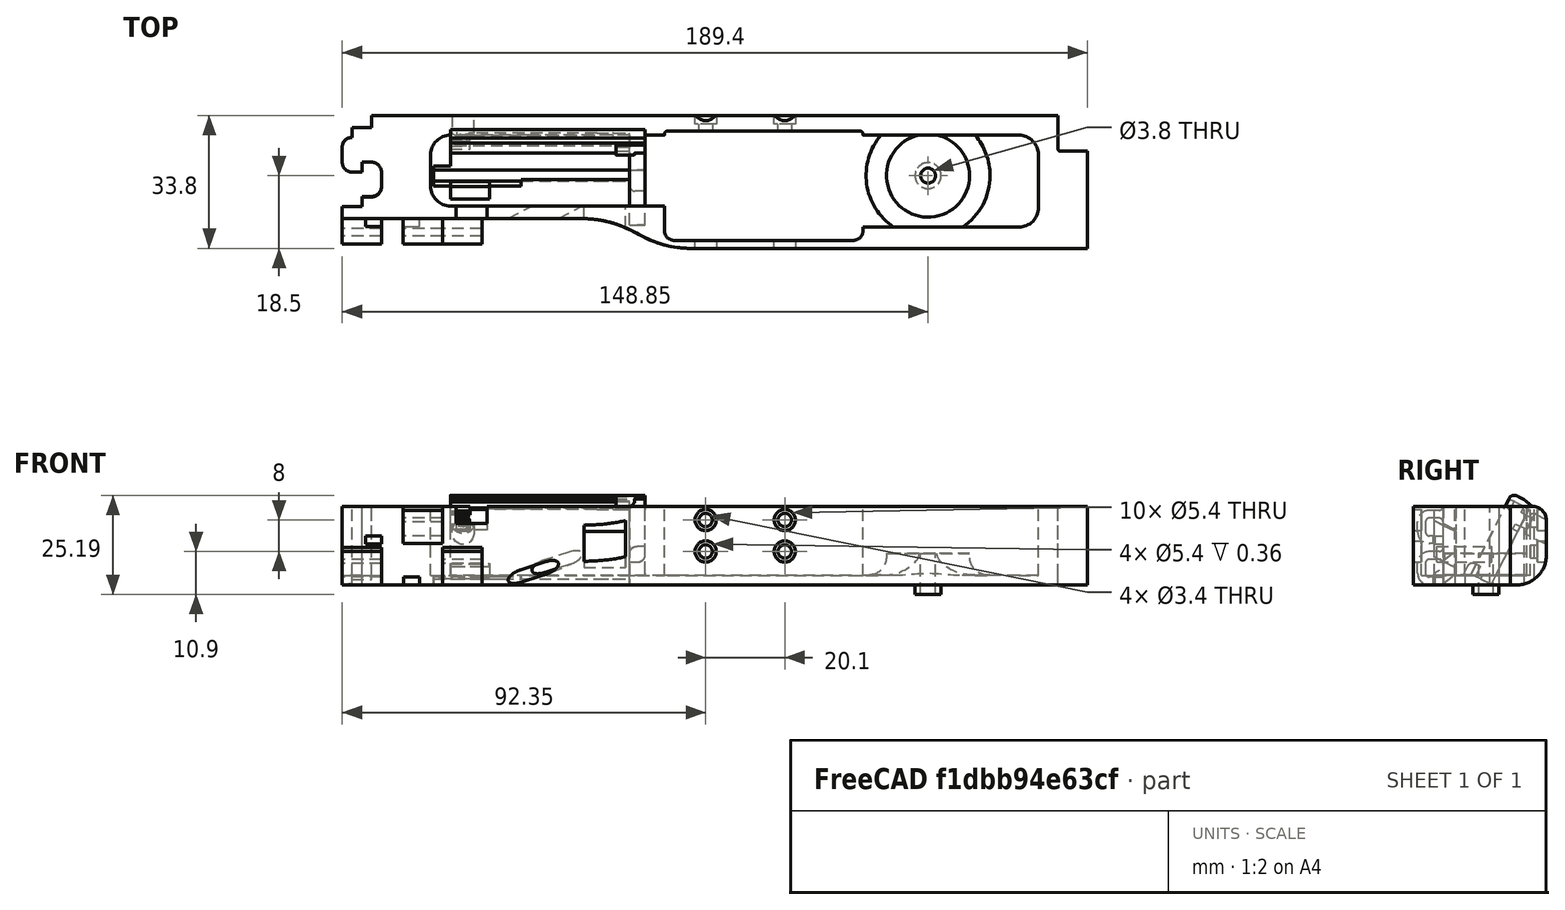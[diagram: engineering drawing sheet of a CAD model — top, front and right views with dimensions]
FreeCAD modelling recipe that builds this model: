
FCSTD DOCUMENT  (FreeCAD 0.19R0.19.2)
Label: v0_9994
License: All rights reserved
LicenseURL: http://en.wikipedia.org/wiki/All_rights_reserved
objects: Sketcher::SketchObject×44, Part::Extrusion×35, Part::MultiFuse×22, Part::Box×18, Part::Cut×15, Part::Fillet×13, App::MeasureDistance×10, Part::Cylinder×4, Part::Revolution×1, Mesh::Feature×1
note: 152 computed .brp shape members not serialized (recipe doc carries the construction recipe); baked Part::Feature solids carry a one-line shape summary decoded from their .brp

FEATURE [Sketcher::SketchObject] Sketch
  FullyConstrained = true
  sketch-geometry (36):
    g0: LineSegment StartX=0 StartY=0 StartZ=0 EndX=154.4 EndY=0 EndZ=0
    g1: LineSegment StartX=154.4 StartY=0 StartZ=0 EndX=154.4 EndY=-7.6 EndZ=0
    g2: LineSegment StartX=32.5209 StartY=-26.2 StartZ=0 EndX=-7.5 EndY=-26.2 EndZ=0
    g3-g7: Circle x5 (B-spline internal-alignment scaffolding for g8; pole/knot coordinates omitted)
    g8: BSplineCurve PolesCount=5 KnotsCount=3 Degree=3 IsPeriodic=0
    g9: GeomPoint X=61.85 Y=-33.8 Z=0
    g10: GeomPoint X=47.185 Y=-29.9 Z=0
    g11: GeomPoint X=32.5209 Y=-26.2 Z=0
    g12: Circle CenterX=121.35 CenterY=-14.3 CenterZ=0 NormalX=0 NormalY=0 NormalZ=1 AngleXU=0 Radius=3.25
    g13: LineSegment StartX=-7.5 StartY=-26.2 StartZ=0 EndX=-27.5 EndY=-26.2 EndZ=0
    g14: LineSegment StartX=-20 StartY=0 StartZ=0 EndX=0 EndY=0 EndZ=0
    g15: LineSegment StartX=-25 StartY=-3.1 StartZ=0 EndX=-20 EndY=-3.1 EndZ=0
    g16: LineSegment StartX=-25 StartY=-3.1 StartZ=0 EndX=-25 EndY=-5.6 EndZ=0
    g17: LineSegment StartX=-27.5 StartY=-8.1 StartZ=0 EndX=-27.5 EndY=-11.85 EndZ=0
    g18: ArcOfCircle CenterX=-25 CenterY=-8.1 CenterZ=0 NormalX=0 NormalY=0 NormalZ=1 AngleXU=0 Radius=2.5 StartAngle=1.5708 EndAngle=3.14159
    g19: LineSegment StartX=-25 StartY=-14.35 StartZ=0 EndX=-22.5 EndY=-14.35 EndZ=0
    g20: ArcOfCircle CenterX=-25 CenterY=-11.85 CenterZ=0 NormalX=0 NormalY=0 NormalZ=1 AngleXU=0 Radius=2.5 StartAngle=3.14159 EndAngle=4.71239
    g21: LineSegment StartX=-22.5 StartY=-14.35 StartZ=0 EndX=-22.5 EndY=-11.85 EndZ=0
    g22: LineSegment StartX=-22.5 StartY=-11.85 StartZ=0 EndX=-20 EndY=-11.85 EndZ=0
    g23: ArcOfCircle CenterX=-20 CenterY=-14.35 CenterZ=0 NormalX=0 NormalY=0 NormalZ=1 AngleXU=0 Radius=2.5 StartAngle=8e-16 EndAngle=1.5708
    g24: LineSegment StartX=-17.5 StartY=-14.35 StartZ=0 EndX=-17.5 EndY=-18.1 EndZ=0
    g25: ArcOfCircle CenterX=-20 CenterY=-18.1 CenterZ=0 NormalX=0 NormalY=0 NormalZ=1 AngleXU=0 Radius=2.5 StartAngle=4.71239 EndAngle=6.28319
    g26: LineSegment StartX=-22.5 StartY=-20.6 StartZ=0 EndX=-20 EndY=-20.6 EndZ=0
    g27: LineSegment StartX=-22.5 StartY=-20.6 StartZ=0 EndX=-22.5 EndY=-23.1 EndZ=0
    g28: LineSegment StartX=-27.5 StartY=-23.1 StartZ=0 EndX=-22.5 EndY=-23.1 EndZ=0
    g29: LineSegment StartX=-20 StartY=-3.1 StartZ=0 EndX=-20 EndY=0 EndZ=0
    g30: LineSegment StartX=-27.5 StartY=-23.1 StartZ=0 EndX=-27.5 EndY=-26.2 EndZ=0
    g31: LineSegment StartX=154.4 StartY=-7.6 StartZ=0 EndX=154.4 EndY=-8.6 EndZ=0
    g32: ArcOfCircle CenterX=154.9 CenterY=-8.6 CenterZ=0 NormalX=0 NormalY=0 NormalZ=1 AngleXU=0 Radius=0.5 StartAngle=3.14159 EndAngle=4.71239
    g33: LineSegment StartX=154.9 StartY=-9.1 StartZ=0 EndX=161.9 EndY=-9.1 EndZ=0
    g34: LineSegment StartX=161.9 StartY=-9.1 StartZ=0 EndX=161.9 EndY=-33.8 EndZ=0
    g35: LineSegment StartX=161.9 StartY=-33.8 StartZ=0 EndX=61.85 EndY=-33.8 EndZ=0
  constraints (72):
    c: PointOnObject(g0,g-2)
    c: Horizontal(g0)
    c: Distance(g0) = 154.4
    c: DistanceY(g-1,g0) = 0
    c: Vertical(g1)
    c: Distance(g1) = 7.6
    c: Coincident(g1,g0)
    c: Horizontal(g2)
    c: Block(g2)
    c: Weight(g3) = 1
    c: Coincident(g8,g2)
    c: InternalAlignment(g3-g7 -> g8) x5
    c: InternalAlignment(g9,g8)
    c: InternalAlignment(g10,g8)
    c: InternalAlignment(g11,g8)
    c: Block(g12)
    c: Coincident(g13,g2)
    c: Horizontal(g13)
    c: Distance(g13) = 20
    c: Horizontal(g14)
    c: Distance(g14) = 20
    c: Coincident(g14,g0)
    c: Horizontal(g15)
    c: Vertical(g16)
    c: Coincident(g16,g15)
    c: Vertical(g17)
    c: Coincident(g18,g16)
    c: Block(g18)
    c: Coincident(g17,g18)
    c: Horizontal(g19)
    c: Coincident(g20,g17)
    c: Block(g20)
    c: Block(g19)
    c: Vertical(g21)
    c: Coincident(g21,g19)
    c: Horizontal(g22)
    c: Coincident(g22,g21)
    c: Coincident(g23,g22)
    c: Vertical(g24)
    c: Block(g23)
    c: Coincident(g24,g23)
    c: Coincident(g25,g24)
    c: Block(g25)
    c: Horizontal(g26)
    c: Coincident(g26,g25)
    c: Vertical(g27)
    c: Coincident(g27,g26)
    c: Horizontal(g28)
    c: Coincident(g28,g27)
    c: Block(g15)
    c: Block(g28)
    c: Coincident(g29,g15)
    c: Coincident(g29,g14)
    c: Vertical(g29)
    c: Coincident(g30,g28)
    c: Coincident(g30,g13)
    c: Vertical(g30)
    c: Vertical(g31)
    c: Distance(g31) = 1
    c: Coincident(g31,g1)
    c: Coincident(g32,g31)
    c: Block(g32)
    c: Coincident(g33,g32)
    c: Horizontal(g33)
    c: Coincident(g34,g33)
    c: Vertical(g34)
    c: Block(g34)
    c: Coincident(g35,g34)
    c: Horizontal(g35)
    c: Block(g35)
    c: Coincident(g8,g35)
    c: Block(g8)
FEATURE [Part::Extrusion] Extrude  label="mainBodyBaseExtrude"
  Base = -> Sketch
  Dir = (0,0,1)
  DirMode = 2
  FaceMakerClass = Part::FaceMakerBullseye
  LengthFwd = 2.4
  LengthRev = 0
  Solid = true
  Symmetric = false
FEATURE [Sketcher::SketchObject] Sketch001
  FullyConstrained = true
  sketch-geometry (75):
    g0: ArcOfCircle CenterX=144.4 CenterY=-10 CenterZ=0 NormalX=0 NormalY=0 NormalZ=1 AngleXU=0 Radius=5 StartAngle=4.345e-13 EndAngle=1.5708
    g1: LineSegment StartX=32.5209 StartY=-26.2 StartZ=0 EndX=-7.49911 EndY=-26.2 EndZ=0
    g2: LineSegment StartX=0 StartY=0 StartZ=0 EndX=154.4 EndY=0 EndZ=0
    g3-g7: Circle x5 (B-spline internal-alignment scaffolding for g8; pole/knot coordinates omitted)
    g8: BSplineCurve PolesCount=5 KnotsCount=3 Degree=3 IsPeriodic=0
    g9: GeomPoint X=61.85 Y=-33.8 Z=0
    g10: GeomPoint X=47.1857 Y=-29.9 Z=0
    g11: GeomPoint X=32.5209 Y=-26.2 Z=0
    g12: LineSegment StartX=154.4 StartY=0 StartZ=0 EndX=154.4 EndY=-7.6 EndZ=0
    g13: LineSegment StartX=20 StartY=-5 StartZ=0 EndX=54.35 EndY=-5 EndZ=0
    g14: LineSegment StartX=104.85 StartY=-5 StartZ=0 EndX=144.4 EndY=-5 EndZ=0
    g15: LineSegment StartX=54.35 StartY=-23 StartZ=0 EndX=20 EndY=-23 EndZ=0
    g16: LineSegment StartX=-27.4991 StartY=-26.2 StartZ=0 EndX=-7.49911 EndY=-26.2 EndZ=0
    g17: LineSegment StartX=-20 StartY=0 StartZ=0 EndX=0 EndY=0 EndZ=0
    g18: LineSegment StartX=-27.4991 StartY=-23.2 StartZ=0 EndX=-22.5 EndY=-23.2 EndZ=0
    g19: LineSegment StartX=-22.5 StartY=-20.7 StartZ=0 EndX=-22.5 EndY=-23.2 EndZ=0
    g20: LineSegment StartX=-22.5 StartY=-20.7 StartZ=0 EndX=-20 EndY=-20.7 EndZ=0
    g21: ArcOfCircle CenterX=-20 CenterY=-18.2 CenterZ=0 NormalX=0 NormalY=0 NormalZ=1 AngleXU=0 Radius=2.5 StartAngle=4.71239 EndAngle=6.28319
    g22: LineSegment StartX=-17.5 StartY=-14.4 StartZ=0 EndX=-17.5 EndY=-18.2 EndZ=0
    g23: ArcOfCircle CenterX=-20 CenterY=-14.4 CenterZ=0 NormalX=0 NormalY=0 NormalZ=1 AngleXU=0 Radius=2.5 StartAngle=9e-16 EndAngle=1.5708
    g24: LineSegment StartX=-22.5 StartY=-11.9 StartZ=0 EndX=-20 EndY=-11.9 EndZ=0
    g25: LineSegment StartX=-22.5 StartY=-14.4 StartZ=0 EndX=-22.5 EndY=-11.9 EndZ=0
    g26: LineSegment StartX=-25 StartY=-14.4 StartZ=0 EndX=-22.5 EndY=-14.4 EndZ=0
    g27: ArcOfCircle CenterX=-25 CenterY=-11.9 CenterZ=0 NormalX=0 NormalY=0 NormalZ=1 AngleXU=0 Radius=2.5 StartAngle=3.14159 EndAngle=4.71239
    g28: LineSegment StartX=-27.5 StartY=-8.1 StartZ=0 EndX=-27.5 EndY=-11.9 EndZ=0
    g29: ArcOfCircle CenterX=-25 CenterY=-8.1 CenterZ=0 NormalX=0 NormalY=0 NormalZ=1 AngleXU=0 Radius=2.5 StartAngle=1.5708 EndAngle=3.14159
    g30: LineSegment StartX=-25 StartY=-3.1 StartZ=0 EndX=-25 EndY=-5.6 EndZ=0
    g31: LineSegment StartX=-20 StartY=-3.1 StartZ=0 EndX=-25 EndY=-3.1 EndZ=0
    g32: LineSegment StartX=-20 StartY=0 StartZ=0 EndX=-20 EndY=-3.1 EndZ=0
    g33: LineSegment StartX=-27.4991 StartY=-26.2 StartZ=0 EndX=-27.4991 EndY=-23.2 EndZ=0
    g34: LineSegment StartX=4.09e-14 StartY=-5 StartZ=0 EndX=20 EndY=-5 EndZ=0
    g35: ArcOfCircle CenterX=7.1e-15 CenterY=-18 CenterZ=0 NormalX=0 NormalY=0 NormalZ=1 AngleXU=0 Radius=5 StartAngle=3.14159 EndAngle=4.71239
    g36: ArcOfCircle CenterX=4.26e-14 CenterY=-10 CenterZ=0 NormalX=0 NormalY=0 NormalZ=1 AngleXU=0 Radius=5 StartAngle=1.5708 EndAngle=3.14159
    g37: LineSegment StartX=-5 StartY=-18 StartZ=0 EndX=-5 EndY=-10 EndZ=0
    g38: LineSegment StartX=6.2e-15 StartY=-23 StartZ=0 EndX=20 EndY=-23 EndZ=0
    g39: LineSegment StartX=154.4 StartY=-7.6 StartZ=0 EndX=154.4 EndY=-8.6 EndZ=0
    g40: LineSegment StartX=154.9 StartY=-9.1 StartZ=0 EndX=161.9 EndY=-9.1 EndZ=0
    g41: ArcOfCircle CenterX=154.9 CenterY=-8.6 CenterZ=0 NormalX=0 NormalY=0 NormalZ=1 AngleXU=0 Radius=0.5 StartAngle=3.14159 EndAngle=4.71299
    g42: LineSegment StartX=104.85 StartY=-28.3916 StartZ=0 EndX=144.408 EndY=-28.3916 EndZ=0
    g43: LineSegment StartX=149.4 StartY=-10 StartZ=0 EndX=149.4 EndY=-23.4 EndZ=0
    g44: ArcOfCircle CenterX=144.408 CenterY=-23.4 CenterZ=0 NormalX=0 NormalY=0 NormalZ=1 AngleXU=0 Radius=4.99164 StartAngle=4.71239 EndAngle=6.28319
    g45: LineSegment StartX=104.85 StartY=-28.3916 StartZ=0 EndX=104.85 EndY=-28.7833 EndZ=0
    g46: LineSegment StartX=54.35 StartY=-28.7916 StartZ=0 EndX=54.35 EndY=-23 EndZ=0
    g47: LineSegment StartX=161.9 StartY=-33.8 StartZ=0 EndX=161.9 EndY=-9.1 EndZ=0
    g48: LineSegment StartX=61.85 StartY=-33.8 StartZ=0 EndX=161.9 EndY=-33.8 EndZ=0
    g49: Circle CenterX=54.35 CenterY=-28.7916 CenterZ=0 NormalX=0 NormalY=0 NormalZ=1 AngleXU=0 Radius=1
    g50: Circle CenterX=54.35 CenterY=-31.7916 CenterZ=0 NormalX=0 NormalY=0 NormalZ=1 AngleXU=0 Radius=1
    g51: Circle CenterX=57.35 CenterY=-31.7916 CenterZ=0 NormalX=0 NormalY=0 NormalZ=1 AngleXU=0 Radius=1
    g52: BSplineCurve PolesCount=3 KnotsCount=2 Degree=2 IsPeriodic=0
    g53: GeomPoint X=54.35 Y=-28.7916 Z=0
    g54: GeomPoint X=57.35 Y=-31.7916 Z=0
    g55: Circle CenterX=104.85 CenterY=-28.7833 CenterZ=0 NormalX=0 NormalY=0 NormalZ=1 AngleXU=0 Radius=1
    g56: Circle CenterX=104.85 CenterY=-31.7916 CenterZ=0 NormalX=0 NormalY=0 NormalZ=1 AngleXU=0 Radius=1
    g57: Circle CenterX=101.85 CenterY=-31.7916 CenterZ=0 NormalX=0 NormalY=0 NormalZ=1 AngleXU=0 Radius=1
    g58: BSplineCurve PolesCount=3 KnotsCount=2 Degree=2 IsPeriodic=0
    g59: GeomPoint X=104.85 Y=-28.7833 Z=0
    g60: GeomPoint X=101.85 Y=-31.7916 Z=0
    g61: LineSegment StartX=57.35 StartY=-31.7916 StartZ=0 EndX=101.85 EndY=-31.7916 EndZ=0
    g62: Circle CenterX=54.35 CenterY=-5 CenterZ=0 NormalX=0 NormalY=0 NormalZ=1 AngleXU=0 Radius=1
    g63: Circle CenterX=54.35 CenterY=-4 CenterZ=0 NormalX=0 NormalY=0 NormalZ=1 AngleXU=0 Radius=1
    g64: Circle CenterX=55.15 CenterY=-4 CenterZ=0 NormalX=0 NormalY=0 NormalZ=1 AngleXU=0 Radius=1
    g65: BSplineCurve PolesCount=3 KnotsCount=2 Degree=2 IsPeriodic=0
    g66: GeomPoint X=54.35 Y=-5 Z=0
    g67: GeomPoint X=55.15 Y=-4 Z=0
    g68: Circle CenterX=104.85 CenterY=-5 CenterZ=0 NormalX=0 NormalY=0 NormalZ=1 AngleXU=0 Radius=1
    g69: Circle CenterX=104.85 CenterY=-4 CenterZ=0 NormalX=0 NormalY=0 NormalZ=1 AngleXU=0 Radius=1
    g70: Circle CenterX=104.05 CenterY=-4 CenterZ=0 NormalX=0 NormalY=0 NormalZ=1 AngleXU=0 Radius=1
    g71: BSplineCurve PolesCount=3 KnotsCount=2 Degree=2 IsPeriodic=0
    g72: GeomPoint X=104.85 Y=-5 Z=0
    g73: GeomPoint X=104.05 Y=-4 Z=0
    g74: LineSegment StartX=104.05 StartY=-4 StartZ=0 EndX=55.15 EndY=-4 EndZ=0
  constraints (156):
    c: PointOnObject(g2,g-2)
    c: DistanceY(g-1,g2) = 0
    c: Block(g0)
    c: Horizontal(g1)
    c: Distance(g1) = 40.02
    c: Horizontal(g2)
    c: Block(g2)
    c: Weight(g3) = 1
    c: Equal(g3, g4-g7) x4
    c: Coincident(g8,g1)
    c: InternalAlignment(g3-g7 -> g8) x5
    c: InternalAlignment(g9,g8)
    c: InternalAlignment(g10,g8)
    c: InternalAlignment(g11,g8)
    c: Vertical(g12)
    c: Coincident(g12,g2)
    c: Distance(g12) = 7.6
    c: Block(g12)
    c: Horizontal(g13)
    c: Coincident(g14,g0)
    c: Horizontal(g14)
    c: Horizontal(g15)
    c: Horizontal(g16)
    c: Distance(g16) = 20
    c: Coincident(g1,g16)
    c: Horizontal(g17)
    c: Distance(g17) = 20
    c: Coincident(g17,g2)
    c: Horizontal(g31)
    c: Vertical(g30)
    c: Coincident(g29,g30)
    c: Vertical(g28)
    c: Block(g29)
    c: Coincident(g27,g28)
    c: Block(g27)
    c: Horizontal(g26)
    c: Coincident(g26,g27)
    c: Vertical(g25)
    c: Coincident(g25,g26)
    c: Horizontal(g24)
    c: Coincident(g23,g24)
    c: Block(g23)
    c: Vertical(g22)
    c: Coincident(g21,g22)
    c: Block(g21)
    c: Horizontal(g20)
    c: Coincident(g20,g21)
    c: Vertical(g19)
    c: Coincident(g19,g20)
    c: Horizontal(g18)
    c: Coincident(g18,g19)
    c: Coincident(g32,g17)
    c: Coincident(g32,g31)
    c: Vertical(g32)
    c: Coincident(g33,g16)
    c: Coincident(g33,g18)
    c: Vertical(g33)
    c: Block(g33)
    c: Block(g18)
    c: Block(g22)
    c: Block(g26)
    c: Block(g25)
    c: Block(g24)
    c: Block(g28)
    c: Block(g31)
    c: Block(g30)
    c: Horizontal(g34)
    c: Distance(g34) = 20
    c: Block(g35)
    c: Block(g36)
    c: Coincident(g37,g35)
    c: Coincident(g37,g36)
    c: Vertical(g37)
    c: Coincident(g38,g35)
    c: Coincident(g38,g15)
    c: Horizontal(g38)
    c: Block(g38)
    c: Block(g34)
    c: Block(g13)
    c: Vertical(g39)
    c: Distance(g39) = 1
    c: Coincident(g39,g12)
    c: Horizontal(g40)
    c: Coincident(g41,g39)
    c: Coincident(g41,g40)
    c: Block(g39)
    c: Block(g41)
    c: Horizontal(g42)
    c: Vertical(g43)
    c: Distance(g43) = 13.4
    c: Coincident(g43,g0)
    c: Block(g42)
    c: Block(g43)
    c: Coincident(g44,g43)
    c: Coincident(g44,g42)
    c: Block(g44)
    c: Distance(g15) = 34.35
    c: Coincident(g45,g42)
    c: Vertical(g45)
    c: Coincident(g46,g15)
    c: Vertical(g46)
    c: Coincident(g47,g40)
    c: Vertical(g47)
    c: Block(g47)
    c: Coincident(g48,g47)
    c: Horizontal(g48)
    c: Block(g48)
    c: Coincident(g8,g48)
    c: Block(g8)
    c: Coincident(g52,g46)
    c: Weight(g49) = 1
    c: Equal(g49,g50)
    c: Equal(g49,g51)
    c: InternalAlignment(g49,g52)
    c: InternalAlignment(g50,g52)
    c: InternalAlignment(g51,g52)
    c: InternalAlignment(g53,g52)
    c: InternalAlignment(g54,g52)
    c: Coincident(g58,g45)
    c: Weight(g55) = 1
    c: Equal(g55,g56)
    c: Equal(g55,g57)
    c: InternalAlignment(g55,g58)
    c: InternalAlignment(g56,g58)
    c: InternalAlignment(g57,g58)
    c: InternalAlignment(g59,g58)
    c: InternalAlignment(g60,g58)
    c: Block(g58)
    c: Block(g52)
    c: Coincident(g61,g52)
    c: Coincident(g61,g58)
    c: Horizontal(g61)
    c: Block(g14)
    c: Coincident(g65,g13)
    c: Weight(g62) = 1
    c: Equal(g62,g63)
    c: Equal(g62,g64)
    c: InternalAlignment(g62,g65)
    c: InternalAlignment(g63,g65)
    c: InternalAlignment(g64,g65)
    c: InternalAlignment(g66,g65)
    c: InternalAlignment(g67,g65)
    c: Block(g65)
    c: Coincident(g71,g14)
    c: Weight(g68) = 1
    c: Equal(g68,g69)
    c: Equal(g68,g70)
    c: InternalAlignment(g68,g71)
    c: InternalAlignment(g69,g71)
    c: InternalAlignment(g70,g71)
    c: InternalAlignment(g72,g71)
    c: InternalAlignment(g73,g71)
    c: Block(g71)
    c: Coincident(g74,g71)
    c: Coincident(g74,g65)
    c: Horizontal(g74)
FEATURE [Sketcher::SketchObject] Sketch005
  FullyConstrained = true
  Placement = pos=(0,0,0) rot=(1,0,0;1.5708rad)
  sketch-geometry (4):
    g0: Circle CenterX=84.95 CenterY=16.5 CenterZ=0 NormalX=0 NormalY=0 NormalZ=1 AngleXU=0 Radius=1.7
    g1: Circle CenterX=84.95 CenterY=8.5 CenterZ=0 NormalX=0 NormalY=0 NormalZ=1 AngleXU=0 Radius=1.7
    g2: Circle CenterX=64.85 CenterY=8.5 CenterZ=0 NormalX=0 NormalY=0 NormalZ=1 AngleXU=0 Radius=1.7
    g3: Circle CenterX=64.85 CenterY=16.5 CenterZ=0 NormalX=0 NormalY=0 NormalZ=1 AngleXU=0 Radius=1.7
  constraints (4):
    c: Block(g0)
    c: Block(g1)
    c: Block(g2)
    c: Block(g3)
FEATURE [Part::Extrusion] Extrude004  label="removeFromMainBodyToCreateScrewHolesForSolenoidExtrude004"
  Base = -> Sketch005
  Dir = (0,-1,1.1e-15)
  DirMode = 2
  FaceMakerClass = Part::FaceMakerBullseye
  LengthFwd = 10
  LengthRev = 0
  Solid = true
  Symmetric = false
FEATURE [Sketcher::SketchObject] Sketch004
  FullyConstrained = true
  Placement = pos=(0,0,0) rot=(1,0,0;1.5708rad)
  sketch-geometry (12):
    g0: LineSegment StartX=15.75 StartY=2.5 StartZ=0 EndX=15.75 EndY=0 EndZ=0
    g1: Circle CenterX=15.75 CenterY=2.5 CenterZ=0 NormalX=0 NormalY=0 NormalZ=1 AngleXU=0 Radius=1
    g2: Circle CenterX=10.55 CenterY=2.5 CenterZ=0 NormalX=0 NormalY=0 NormalZ=1 AngleXU=0 Radius=1
    g3: Circle CenterX=10.55 CenterY=8 CenterZ=0 NormalX=0 NormalY=0 NormalZ=1 AngleXU=0 Radius=1
    g4: BSplineCurve PolesCount=3 KnotsCount=2 Degree=2 IsPeriodic=0
    g5: GeomPoint X=15.75 Y=2.5 Z=0
    g6: GeomPoint X=10.55 Y=8 Z=0
    g7: LineSegment StartX=1.9 StartY=8 StartZ=0 EndX=10.55 EndY=8 EndZ=0
    g8: LineSegment StartX=1.9 StartY=-2.4 StartZ=0 EndX=1.9 EndY=8 EndZ=0
    g9: LineSegment StartX=3.30092 StartY=-2.4 StartZ=0 EndX=3.30092 EndY=0 EndZ=0
    g10: LineSegment StartX=15.75 StartY=0 StartZ=0 EndX=3.30092 EndY=0 EndZ=0
    g11: LineSegment StartX=3.30092 StartY=-2.4 StartZ=0 EndX=1.9 EndY=-2.4 EndZ=0
  constraints (26):
    c: Vertical(g0)
    c: Distance(g0) = 2.5
    c: Coincident(g4,g0)
    c: Weight(g1) = 1
    c: Equal(g1,g2)
    c: Equal(g1,g3)
    c: InternalAlignment(g1,g4)
    c: InternalAlignment(g2,g4)
    c: InternalAlignment(g3,g4)
    c: InternalAlignment(g5,g4)
    c: InternalAlignment(g6,g4)
    c: Block(g4)
    c: Coincident(g7,g4)
    c: Horizontal(g7)
    c: Vertical(g8)
    c: Coincident(g8,g7)
    c: Block(g8)
    c: Vertical(g9)
    c: Coincident(g10,g0)
    c: PointOnObject(g10,g-1)
    c: Horizontal(g10)
    c: Coincident(g10,g9)
    c: Block(g9)
    c: Coincident(g11,g9)
    c: Coincident(g11,g8)
    c: Horizontal(g11)
FEATURE [Sketcher::SketchObject] Sketch007
  FullyConstrained = true
  Placement = pos=(0,-14.3,2.37) rot=(-1,0,0;2.03453rad)
  sketch-geometry (6):
    g0: LineSegment StartX=0 StartY=0 StartZ=0 EndX=45.5 EndY=0 EndZ=0
    g1: LineSegment StartX=0 StartY=0 StartZ=0 EndX=0 EndY=-21.2 EndZ=0
    g2: LineSegment StartX=45.5 StartY=0 StartZ=0 EndX=49.5 EndY=0 EndZ=0
    g3: LineSegment StartX=49.5 StartY=0 StartZ=0 EndX=49.5 EndY=-21.2 EndZ=0
    g4: LineSegment StartX=49.5 StartY=-21.2 StartZ=0 EndX=0 EndY=-21.2 EndZ=0
    g5: Circle CenterX=3.25 CenterY=-18.05 CenterZ=0 NormalX=0 NormalY=0 NormalZ=1 AngleXU=0 Radius=1.6
  constraints (15):
    c: Coincident(g0,g-1)
    c: Horizontal(g0)
    c: Distance(g0) = 45.5
    c: Coincident(g1,g0)
    c: Vertical(g1)
    c: Horizontal(g2)
    c: Distance(g2) = 4
    c: Coincident(g2,g0)
    c: Coincident(g3,g2)
    c: Vertical(g3)
    c: Block(g3)
    c: Coincident(g4,g3)
    c: Horizontal(g4)
    c: Coincident(g4,g1)
    c: Block(g5)
FEATURE [Part::Extrusion] Extrude005  label="solenoidDriverHolderExtrude005"
  Base = -> Sketch007
  Dir = (0,0.894389,-0.447291)
  DirMode = 2
  FaceMakerClass = Part::FaceMakerBullseye
  LengthFwd = 10
  LengthRev = 0
  Placement = pos=(0,0,-2) rot=(0,0,1;0rad)
  Solid = true
  Symmetric = false
FEATURE [Sketcher::SketchObject] Sketch008
  FullyConstrained = false
  Placement = pos=(0,-4.3,-2.6) rot=(-1,0,0;2.03453rad)
  sketch-geometry (1):
    g0: Circle CenterX=42.25 CenterY=-3.15 CenterZ=0 NormalX=0 NormalY=0 NormalZ=1 AngleXU=0 Radius=4.5
FEATURE [Sketcher::SketchObject] Sketch009
  FullyConstrained = true
  Placement = pos=(0,-4.3,-2.6) rot=(-1,0,0;2.03453rad)
  sketch-geometry (1):
    g0: Circle CenterX=3.25 CenterY=-18.0217 CenterZ=0 NormalX=0 NormalY=0 NormalZ=1 AngleXU=0 Radius=2.8
  constraints (1):
    c: Block(g0)
FEATURE [Sketcher::SketchObject] Sketch010
  FullyConstrained = true
  Placement = pos=(0,-14.3,2.37) rot=(-1,0,0;2.03453rad)
  sketch-geometry (1):
    g0: Circle CenterX=3.25 CenterY=-18.05 CenterZ=0 NormalX=0 NormalY=0 NormalZ=1 AngleXU=0 Radius=1.6
  constraints (1):
    c: Block(g0)
FEATURE [Part::Extrusion] Extrude008  label="removeFromScrewHole3"
  Base = -> Sketch010
  Dir = (0,0.894389,-0.447291)
  DirMode = 2
  FaceMakerClass = Part::FaceMakerBullseye
  LengthFwd = -25
  LengthRev = 0
  Placement = pos=(0,4,-4) rot=(0,0,1;0rad)
  Solid = true
  Symmetric = false
FEATURE [Sketcher::SketchObject] Sketch011
  FullyConstrained = true
  Placement = pos=(0,-14.3,2.37) rot=(-1,0,0;2.03453rad)
  sketch-geometry (4):
    g0: LineSegment StartX=49.5 StartY=-21.2 StartZ=0 EndX=49.5 EndY=-22.8 EndZ=0
    g1: LineSegment StartX=49.5 StartY=-22.8 StartZ=0 EndX=0.002238 EndY=-22.8 EndZ=0
    g2: LineSegment StartX=0.002238 StartY=-21.2 StartZ=0 EndX=0.002238 EndY=-22.8 EndZ=0
    g3: LineSegment StartX=49.5 StartY=-21.2 StartZ=0 EndX=0.002238 EndY=-21.2 EndZ=0
  constraints (10):
    c: Vertical(g0)
    c: Distance(g0) = 1.6
    c: Coincident(g1,g0)
    c: Horizontal(g1)
    c: Vertical(g2)
    c: Coincident(g2,g1)
    c: Coincident(g3,g0)
    c: Coincident(g3,g2)
    c: Horizontal(g3)
    c: Block(g3)
FEATURE [Part::Extrusion] Extrude009  label="solenoidDriverTopLipFront"
  Base = -> Sketch011
  Dir = (0,0.894389,-0.447291)
  DirMode = 2
  FaceMakerClass = Part::FaceMakerBullseye
  LengthFwd = -2
  LengthRev = 0
  Placement = pos=(0,-2.9,-0.35) rot=(0,0,1;0rad)
  Solid = true
  Symmetric = false
FEATURE [Sketcher::SketchObject] Sketch012
  FullyConstrained = true
  Placement = pos=(0,-14.3,2.37) rot=(-1,0,0;2.03453rad)
  sketch-geometry (4):
    g0: LineSegment StartX=49.5 StartY=-21.2 StartZ=0 EndX=49.5 EndY=-22.8 EndZ=0
    g1: LineSegment StartX=49.5 StartY=-22.8 StartZ=0 EndX=0.002238 EndY=-22.8 EndZ=0
    g2: LineSegment StartX=0.002238 StartY=-21.2 StartZ=0 EndX=0.002238 EndY=-22.8 EndZ=0
    g3: LineSegment StartX=49.5 StartY=-21.2 StartZ=0 EndX=0.002238 EndY=-21.2 EndZ=0
  constraints (10):
    c: Vertical(g0)
    c: Distance(g0) = 1.6
    c: Coincident(g1,g0)
    c: Horizontal(g1)
    c: Vertical(g2)
    c: Coincident(g2,g1)
    c: Coincident(g3,g0)
    c: Coincident(g3,g2)
    c: Horizontal(g3)
    c: Block(g3)
FEATURE [Part::Extrusion] Extrude010  label="solenoidDriverTopLipLowerExtrude010"
  Base = -> Sketch012
  Dir = (0,0.894389,-0.447291)
  DirMode = 2
  FaceMakerClass = Part::FaceMakerBullseye
  LengthFwd = 5.05
  LengthRev = 0
  Solid = true
  Symmetric = false
FEATURE [Sketcher::SketchObject] Sketch015
  FullyConstrained = true
  Placement = pos=(0,-14.3,2.37) rot=(-1,0,0;2.03453rad)
  sketch-geometry (4):
    g0: LineSegment StartX=0 StartY=1.5 StartZ=0 EndX=0 EndY=0 EndZ=0
    g1: LineSegment StartX=0 StartY=1.5 StartZ=0 EndX=5 EndY=1.5 EndZ=0
    g2: LineSegment StartX=5 StartY=1.5 StartZ=0 EndX=5 EndY=0 EndZ=0
    g3: LineSegment StartX=0 StartY=0 StartZ=0 EndX=5 EndY=0 EndZ=0
  constraints (13):
    c: Vertical(g0)
    c: Distance(g0) = 1.5
    c: Horizontal(g1)
    c: Distance(g1) = 5
    c: Coincident(g1,g0)
    c: Vertical(g2)
    c: Distance(g2) = 1.5
    c: Coincident(g2,g1)
    c: Block(g1)
    c: Block(g2)
    c: Block(g0)
    c: Coincident(g3,g0)
    c: Coincident(g3,g2)
FEATURE [Part::Extrusion] Extrude013  label="solenoidDriverBottomLipTopExtrude012"
  Base = -> Sketch015
  Dir = (0,0.894389,-0.447291)
  DirMode = 2
  FaceMakerClass = Part::FaceMakerBullseye
  LengthFwd = -6.5
  LengthRev = 0
  Placement = pos=(0,-14.15,19.65) rot=(1,0,0;1.5708rad)
  Solid = true
  Symmetric = false
FEATURE [Sketcher::SketchObject] Sketch016
  FullyConstrained = true
  Placement = pos=(0,0,0) rot=(1,0,0;1.5708rad)
  sketch-geometry (4):
    g0: Circle CenterX=84.15 CenterY=16.5 CenterZ=0 NormalX=0 NormalY=0 NormalZ=1 AngleXU=0 Radius=2.7
    g1: Circle CenterX=64.05 CenterY=16.5 CenterZ=0 NormalX=0 NormalY=0 NormalZ=1 AngleXU=0 Radius=2.7
    g2: Circle CenterX=64.05 CenterY=8.5 CenterZ=0 NormalX=0 NormalY=0 NormalZ=1 AngleXU=0 Radius=2.7
    g3: Circle CenterX=84.15 CenterY=8.5 CenterZ=0 NormalX=0 NormalY=0 NormalZ=1 AngleXU=0 Radius=2.7
  constraints (4):
    c: Block(g0)
    c: Block(g1)
    c: Block(g3)
    c: Block(g2)
FEATURE [Part::Extrusion] Extrude014  label="removeFromMainBodyToCreateScrewHoleCounterSinks"
  Base = -> Sketch016
  Dir = (0,-1,1.1e-15)
  DirMode = 2
  FaceMakerClass = Part::FaceMakerBullseye
  LengthFwd = 1.9
  LengthRev = 0
  Placement = pos=(0.8,-0.36,0) rot=(0,0,1;0rad)
  Solid = true
  Symmetric = false
FEATURE [Part::Extrusion] Extrude015  label="removeFromScrewHole2Extrude007"
  Base = -> Sketch009
  Dir = (0,0.894389,-0.447291)
  DirMode = 2
  FaceMakerClass = Part::FaceMakerBullseye
  LengthFwd = 10
  LengthRev = 0
  Placement = pos=(0,-8,2) rot=(0,0,1;0rad)
  Solid = true
  Symmetric = false
FEATURE [Sketcher::SketchObject] Sketch017
  FullyConstrained = true
  Placement = pos=(0,-14.3,2.37) rot=(-1,0,0;2.03453rad)
  sketch-geometry (4):
    g0: LineSegment StartX=0 StartY=1.5 StartZ=0 EndX=0 EndY=0 EndZ=0
    g1: LineSegment StartX=0 StartY=1.5 StartZ=0 EndX=5 EndY=1.5 EndZ=0
    g2: LineSegment StartX=5 StartY=1.5 StartZ=0 EndX=5 EndY=0 EndZ=0
    g3: LineSegment StartX=0 StartY=0 StartZ=0 EndX=5 EndY=0 EndZ=0
  constraints (13):
    c: Vertical(g0)
    c: Distance(g0) = 1.5
    c: Horizontal(g1)
    c: Distance(g1) = 5
    c: Coincident(g1,g0)
    c: Vertical(g2)
    c: Distance(g2) = 1.5
    c: Coincident(g2,g1)
    c: Block(g1)
    c: Block(g2)
    c: Block(g0)
    c: Coincident(g3,g0)
    c: Coincident(g3,g2)
FEATURE [Part::Extrusion] Extrude016  label="solenoidDriverBottomLipTopExtrude013"
  Base = -> Sketch017
  Dir = (0,0.894389,-0.447291)
  DirMode = 2
  FaceMakerClass = Part::FaceMakerBullseye
  LengthFwd = -6.5
  LengthRev = 0
  Placement = pos=(0,-15.45,20.3) rot=(1,0,0;1.5708rad)
  Solid = true
  Symmetric = false
FEATURE [Part::Fillet] Fillet005  label="solenoidDriverBottomLipTopFillet005"
  Base = -> Extrude016
  Edges = 1 edges r=1.4: [Edge6]
FEATURE [Sketcher::SketchObject] Sketch018
  FullyConstrained = true
  Placement = pos=(38.5,-14.3,2.37) rot=(-1,0,0;2.03453rad)
  sketch-geometry (4):
    g0: LineSegment StartX=11 StartY=0 StartZ=0 EndX=11 EndY=1.5 EndZ=0
    g1: LineSegment StartX=11 StartY=0 StartZ=0 EndX=3.6 EndY=0 EndZ=0
    g2: LineSegment StartX=3.6 StartY=0 StartZ=0 EndX=3.6 EndY=1.5 EndZ=0
    g3: LineSegment StartX=11 StartY=1.5 StartZ=0 EndX=3.6 EndY=1.5 EndZ=0
  constraints (12):
    c: PointOnObject(g0,g-1)
    c: Vertical(g0)
    c: Distance(g0) = 1.5
    c: Horizontal(g1)
    c: Distance(g1) = 7.4
    c: Coincident(g1,g0)
    c: Block(g0)
    c: Coincident(g2,g1)
    c: Vertical(g2)
    c: Coincident(g3,g0)
    c: Horizontal(g3)
    c: Coincident(g2,g3)
FEATURE [Part::Extrusion] Extrude017
  Base = -> Sketch018
  Dir = (0,0.894389,-0.447291)
  DirMode = 2
  FaceMakerClass = Part::FaceMakerBullseye
  LengthFwd = 4
  LengthRev = 0
  Placement = pos=(0,-8.212,34.025) rot=(1,0,0;1.5708rad)
  Solid = true
  Symmetric = false
FEATURE [Sketcher::SketchObject] Sketch019
  FullyConstrained = true
  Placement = pos=(0,0,0) rot=(1,0,0;1.5708rad)
  sketch-geometry (4):
    g0: Circle CenterX=84.95 CenterY=8.5 CenterZ=0 NormalX=0 NormalY=0 NormalZ=1 AngleXU=0 Radius=2.7
    g1: Circle CenterX=64.85 CenterY=8.5 CenterZ=0 NormalX=0 NormalY=0 NormalZ=1 AngleXU=0 Radius=2.7
    g2: Circle CenterX=64.85 CenterY=16.5 CenterZ=0 NormalX=0 NormalY=0 NormalZ=1 AngleXU=0 Radius=2.7
    g3: Circle CenterX=84.95 CenterY=16.5 CenterZ=0 NormalX=0 NormalY=0 NormalZ=1 AngleXU=0 Radius=2.7
  constraints (4):
    c: Block(g3)
    c: Block(g2)
    c: Block(g0)
    c: Block(g1)
FEATURE [Part::Extrusion] Extrude019  label="removeSolenoidAdjusterHoles"
  Base = -> Sketch019
  Dir = (0,-1,1.1e-15)
  DirMode = 2
  FaceMakerClass = Part::FaceMakerBullseye
  LengthFwd = 6
  LengthRev = 0
  Placement = pos=(0,-30,0) rot=(0,0,1;0rad)
  Solid = true
  Symmetric = false
FEATURE [Sketcher::SketchObject] Sketch020
  FullyConstrained = true
  Placement = pos=(0,-14.3,2.37) rot=(-1,0,0;2.03453rad)
  sketch-geometry (6):
    g0: LineSegment StartX=45.5 StartY=-21.2 StartZ=0 EndX=49.5 EndY=-21.2 EndZ=0
    g1: LineSegment StartX=45.5 StartY=0 StartZ=0 EndX=49.5 EndY=0 EndZ=0
    g2: LineSegment StartX=49.5 StartY=0 StartZ=0 EndX=49.5 EndY=-21.2 EndZ=0
    g3: LineSegment StartX=4 StartY=0 StartZ=0 EndX=4 EndY=-21.2 EndZ=0
    g4: LineSegment StartX=45.5 StartY=-21.2 StartZ=0 EndX=4 EndY=-21.2 EndZ=0
    g5: LineSegment StartX=4 StartY=0 StartZ=0 EndX=45.5 EndY=0 EndZ=0
  constraints (16):
    c: Horizontal(g0)
    c: Distance(g0) = 4
    c: Horizontal(g1)
    c: Distance(g1) = 4
    c: Coincident(g2,g1)
    c: Coincident(g2,g0)
    c: Vertical(g2)
    c: Block(g2)
    c: Vertical(g3)
    c: Coincident(g4,g0)
    c: Horizontal(g4)
    c: Coincident(g4,g3)
    c: Coincident(g5,g1)
    c: Horizontal(g5)
    c: Block(g3)
    c: Block(g5)
FEATURE [Part::Box] Box  label="Cube"
  AttacherType = Attacher::AttachEngine3D
  Height = 10
  Length = 190
  Placement = pos=(-30,0,0) rot=(0,0,1;0rad)
  Width = 10
FEATURE [Part::Fillet] Fillet008
  Base = -> Box
  Edges = 1 edges r=7.5: [Edge11]
FEATURE [Part::Box] Box001  label="Cube001"
  AttacherType = Attacher::AttachEngine3D
  Height = 10
  Length = 190
  Placement = pos=(-35,0,0) rot=(0,0,1;0rad)
  Width = 10
FEATURE [Part::Cut] Cut  label="filletMain"
  Base = -> Box001
  Placement = pos=(0,-10,0) rot=(0,0,1;0rad)
  Tool = -> Fillet008
FEATURE [Part::Box] Box002  label="Cube002"
  AttacherType = Attacher::AttachEngine3D
  Height = 30
  Length = 190
  Placement = pos=(-20,0,0) rot=(0,0,1;0rad)
  Width = 10
FEATURE [Part::Box] Box003  label="Cube003"
  AttacherType = Attacher::AttachEngine3D
  Height = 10
  Length = 190
  Placement = pos=(-90,-50,-10) rot=(0,0,1;0rad)
  Width = 50
FEATURE [Sketcher::SketchObject] Sketch021
  FullyConstrained = true
  Placement = pos=(0,-14.3,2.37) rot=(-1,0,0;2.03453rad)
  sketch-geometry (6):
    g0: LineSegment StartX=41.65 StartY=-3.15 StartZ=0 EndX=38.95 EndY=-3.15 EndZ=0
    g1: LineSegment StartX=36.25 StartY=-3.15 StartZ=0 EndX=38.95 EndY=-3.15 EndZ=0
    g2: LineSegment StartX=41.65 StartY=-3.15 StartZ=0 EndX=41.65 EndY=-7.15 EndZ=0
    g3: LineSegment StartX=38.95 StartY=-7.15 StartZ=0 EndX=41.65 EndY=-7.15 EndZ=0
    g4: LineSegment StartX=38.95 StartY=-7.15 StartZ=0 EndX=36.25 EndY=-7.15 EndZ=0
    g5: LineSegment StartX=36.25 StartY=-3.15 StartZ=0 EndX=36.25 EndY=-7.15 EndZ=0
  constraints (16):
    c: Horizontal(g0)
    c: Distance(g0) = 2.7
    c: Horizontal(g1)
    c: Distance(g1) = 2.7
    c: Coincident(g1,g0)
    c: Block(g0)
    c: Coincident(g2,g0)
    c: Vertical(g2)
    c: Horizontal(g3)
    c: Coincident(g3,g2)
    c: Horizontal(g4)
    c: Coincident(g5,g1)
    c: Vertical(g5)
    c: Coincident(g5,g4)
    c: Block(g3)
    c: Block(g4)
FEATURE [Sketcher::SketchObject] Sketch022
  FullyConstrained = true
  Placement = pos=(0,-14.3,2.37) rot=(-1,0,0;2.03453rad)
  sketch-geometry (6):
    g0: LineSegment StartX=41.65 StartY=-3.15 StartZ=0 EndX=38.95 EndY=-3.15 EndZ=0
    g1: LineSegment StartX=36.25 StartY=-3.15 StartZ=0 EndX=38.95 EndY=-3.15 EndZ=0
    g2: LineSegment StartX=41.65 StartY=-3.15 StartZ=0 EndX=41.65 EndY=-7.15 EndZ=0
    g3: LineSegment StartX=38.95 StartY=-7.15 StartZ=0 EndX=41.65 EndY=-7.15 EndZ=0
    g4: LineSegment StartX=38.95 StartY=-7.15 StartZ=0 EndX=36.25 EndY=-7.15 EndZ=0
    g5: LineSegment StartX=36.25 StartY=-3.15 StartZ=0 EndX=36.25 EndY=-7.15 EndZ=0
  constraints (16):
    c: Horizontal(g0)
    c: Distance(g0) = 2.7
    c: Horizontal(g1)
    c: Distance(g1) = 2.7
    c: Coincident(g1,g0)
    c: Block(g0)
    c: Coincident(g2,g0)
    c: Vertical(g2)
    c: Horizontal(g3)
    c: Coincident(g3,g2)
    c: Horizontal(g4)
    c: Coincident(g5,g1)
    c: Vertical(g5)
    c: Coincident(g5,g4)
    c: Block(g3)
    c: Block(g4)
FEATURE [Sketcher::SketchObject] Sketch024
  FullyConstrained = true
  Placement = pos=(0,-14.3,2.37) rot=(-1,0,0;2.03453rad)
  sketch-geometry (4):
    g0: LineSegment StartX=49.5 StartY=-21.2 StartZ=0 EndX=49.5 EndY=-22.8 EndZ=0
    g1: LineSegment StartX=49.5 StartY=-22.8 StartZ=0 EndX=0.002238 EndY=-22.8 EndZ=0
    g2: LineSegment StartX=0.002238 StartY=-21.2 StartZ=0 EndX=0.002238 EndY=-22.8 EndZ=0
    g3: LineSegment StartX=49.5 StartY=-21.2 StartZ=0 EndX=0.002238 EndY=-21.2 EndZ=0
  constraints (10):
    c: Vertical(g0)
    c: Distance(g0) = 1.6
    c: Coincident(g1,g0)
    c: Horizontal(g1)
    c: Vertical(g2)
    c: Coincident(g2,g1)
    c: Coincident(g3,g0)
    c: Coincident(g3,g2)
    c: Horizontal(g3)
    c: Block(g3)
FEATURE [Sketcher::SketchObject] Sketch025
  FullyConstrained = true
  Placement = pos=(0,-14.3,2.37) rot=(-1,0,0;2.03453rad)
  sketch-geometry (4):
    g0: LineSegment StartX=0 StartY=1.5 StartZ=0 EndX=0 EndY=0 EndZ=0
    g1: LineSegment StartX=0 StartY=1.5 StartZ=0 EndX=5 EndY=1.5 EndZ=0
    g2: LineSegment StartX=5 StartY=1.5 StartZ=0 EndX=5 EndY=0 EndZ=0
    g3: LineSegment StartX=0 StartY=0 StartZ=0 EndX=5 EndY=0 EndZ=0
  constraints (13):
    c: Vertical(g0)
    c: Distance(g0) = 1.5
    c: Horizontal(g1)
    c: Distance(g1) = 5
    c: Coincident(g1,g0)
    c: Vertical(g2)
    c: Distance(g2) = 1.5
    c: Coincident(g2,g1)
    c: Block(g1)
    c: Block(g2)
    c: Block(g0)
    c: Coincident(g3,g0)
    c: Coincident(g3,g2)
FEATURE [Part::Extrusion] Extrude022  label="solenoidDriverBottomLipTopExtrude014"
  Base = -> Sketch025
  Dir = (0,0.894389,-0.447291)
  DirMode = 2
  FaceMakerClass = Part::FaceMakerBullseye
  LengthFwd = -6.5
  LengthRev = 0
  Placement = pos=(0,-15.45,20.3) rot=(1,0,0;1.5708rad)
  Solid = true
  Symmetric = false
FEATURE [Part::Fillet] Fillet013  label="solenoidDriverBottomLipTopFillet006"
  Base = -> Extrude022
  Edges = 1 edges r=1.4: [Edge6]
  Placement = pos=(5,0,0) rot=(0,0,1;0rad)
FEATURE [Sketcher::SketchObject] Sketch026
  FullyConstrained = true
  Placement = pos=(0,-14.3,2.37) rot=(-1,0,0;2.03453rad)
  sketch-geometry (4):
    g0: LineSegment StartX=0 StartY=1.5 StartZ=0 EndX=0 EndY=0 EndZ=0
    g1: LineSegment StartX=0 StartY=1.5 StartZ=0 EndX=5 EndY=1.5 EndZ=0
    g2: LineSegment StartX=5 StartY=1.5 StartZ=0 EndX=5 EndY=0 EndZ=0
    g3: LineSegment StartX=0 StartY=0 StartZ=0 EndX=5 EndY=0 EndZ=0
  constraints (13):
    c: Vertical(g0)
    c: Distance(g0) = 1.5
    c: Horizontal(g1)
    c: Distance(g1) = 5
    c: Coincident(g1,g0)
    c: Vertical(g2)
    c: Distance(g2) = 1.5
    c: Coincident(g2,g1)
    c: Block(g1)
    c: Block(g2)
    c: Block(g0)
    c: Coincident(g3,g0)
    c: Coincident(g3,g2)
FEATURE [Part::Extrusion] Extrude023  label="solenoidDriverBottomLipTopExtrude015"
  Base = -> Sketch026
  Dir = (0,0.894389,-0.447291)
  DirMode = 2
  FaceMakerClass = Part::FaceMakerBullseye
  LengthFwd = -6.5
  LengthRev = 0
  Placement = pos=(5,-14.15,19.65) rot=(1,0,0;1.5708rad)
  Solid = true
  Symmetric = false
FEATURE [Sketcher::SketchObject] Sketch027
  FullyConstrained = true
  Placement = pos=(0,-14.3,2.37) rot=(-1,0,0;2.03453rad)
  sketch-geometry (5):
    g0: LineSegment StartX=45.5 StartY=-21.2 StartZ=0 EndX=49.5 EndY=-21.2 EndZ=0
    g1: LineSegment StartX=49.5 StartY=0 StartZ=0 EndX=49.5 EndY=-21.2 EndZ=0
    g2: LineSegment StartX=49.5 StartY=0 StartZ=0 EndX=49.5 EndY=1.6 EndZ=0
    g3: LineSegment StartX=45.5 StartY=-21.2 StartZ=0 EndX=45.5 EndY=1.6 EndZ=0
    g4: LineSegment StartX=49.5 StartY=1.6 StartZ=0 EndX=45.5 EndY=1.6 EndZ=0
  constraints (14):
    c: Horizontal(g0)
    c: Distance(g0) = 4
    c: Coincident(g1,g0)
    c: Vertical(g1)
    c: Block(g1)
    c: Vertical(g2)
    c: Distance(g2) = 1.6
    c: Block(g2)
    c: Coincident(g3,g0)
    c: Vertical(g3)
    c: Coincident(g4,g2)
    c: Horizontal(g4)
    c: Block(g0)
    c: Coincident(g3,g4)
FEATURE [Part::Extrusion] Extrude024
  Base = -> Sketch027
  Dir = (0,0.894389,-0.447291)
  DirMode = 2
  FaceMakerClass = Part::FaceMakerBullseye
  LengthFwd = 6.34
  LengthRev = 0
  Placement = pos=(0,-5.59,1) rot=(0,0,1;0rad)
  Solid = true
  Symmetric = false
FEATURE [Part::Fillet] Fillet014  label="solenoidDriverSideBarFillet014"
  Base = -> Extrude024
  Edges = 1 edges r=1.4: [Edge14]
  Placement = pos=(0,0.9,-0.45) rot=(0,0,1;0rad)
FEATURE [Part::Revolution] Revolve  label="mainScrewStandRevolve"
  Angle = 360
  Axis = (0,0,1)
  Base = (0,0,0)
  FaceMakerClass = Part::FaceMakerBullseye
  Placement = pos=(121.35,-15.3,0) rot=(0,0,1;0rad)
  Solid = true
  Source = -> Sketch004
  Symmetric = false
FEATURE [Part::Extrusion] Extrude021  label="solenoidDriverTopLipLowerExtrude011"
  Base = -> Sketch024
  Dir = (0,0.894389,-0.447291)
  DirMode = 2
  FaceMakerClass = Part::FaceMakerBullseye
  LengthFwd = 5.05
  LengthRev = 0
  Solid = true
  Symmetric = false
FEATURE [Part::Fillet] Fillet012  label="solenoidDriverTopLipLowerFillet004"
  Base = -> Extrude021
  Edges = 1 edges r=1.2: [Edge7]
  Placement = pos=(0,-0.9,-1.35) rot=(0,0,1;0rad)
FEATURE [Part::Fillet] Fillet003  label="solenoidDriverTopLipLowerFillet003"
  Base = -> Extrude010
  Edges = 1 edges r=1.2: [Edge7]
  Placement = pos=(0,-3,-0.3) rot=(0,0,1;0rad)
FEATURE [Part::Extrusion] Extrude025  label="mainBodyUpperExtrude025"
  Base = -> Sketch001
  Dir = (0,0,1)
  DirMode = 2
  FaceMakerClass = Part::FaceMakerBullseye
  LengthFwd = 20
  LengthRev = 0
  Solid = true
  Symmetric = false
FEATURE [Part::MultiFuse] Fusion  label="solenoidDriverBottomLipFusion"
  Placement = pos=(0,-1.6,0) rot=(0,0,1;0rad)
  Shapes = -> [Fillet005,Fillet013,Extrude023,Extrude013]
FEATURE [Sketcher::SketchObject] Sketch028
  FullyConstrained = true
  Placement = pos=(0,-14.3,2.37) rot=(-1,0,0;2.03453rad)
  sketch-geometry (4):
    g0: LineSegment StartX=0 StartY=1.5 StartZ=0 EndX=0 EndY=0 EndZ=0
    g1: LineSegment StartX=0 StartY=1.5 StartZ=0 EndX=5 EndY=1.5 EndZ=0
    g2: LineSegment StartX=5 StartY=1.5 StartZ=0 EndX=5 EndY=0 EndZ=0
    g3: LineSegment StartX=0 StartY=0 StartZ=0 EndX=5 EndY=0 EndZ=0
  constraints (13):
    c: Vertical(g0)
    c: Distance(g0) = 1.5
    c: Horizontal(g1)
    c: Distance(g1) = 5
    c: Coincident(g1,g0)
    c: Vertical(g2)
    c: Distance(g2) = 1.5
    c: Coincident(g2,g1)
    c: Block(g1)
    c: Block(g2)
    c: Block(g0)
    c: Coincident(g3,g0)
    c: Coincident(g3,g2)
FEATURE [Part::Extrusion] Extrude026  label="solenoidDriverBottomLipTopExtrude016"
  Base = -> Sketch028
  Dir = (0,0.894389,-0.447291)
  DirMode = 2
  FaceMakerClass = Part::FaceMakerBullseye
  LengthFwd = -6.5
  LengthRev = 0
  Placement = pos=(5,-14.15,19.65) rot=(1,0,0;1.5708rad)
  Solid = true
  Symmetric = false
FEATURE [Sketcher::SketchObject] Sketch029
  FullyConstrained = true
  Placement = pos=(0,-14.3,2.37) rot=(-1,0,0;2.03453rad)
  sketch-geometry (4):
    g0: LineSegment StartX=0 StartY=1.5 StartZ=0 EndX=0 EndY=0 EndZ=0
    g1: LineSegment StartX=0 StartY=1.5 StartZ=0 EndX=5 EndY=1.5 EndZ=0
    g2: LineSegment StartX=5 StartY=1.5 StartZ=0 EndX=5 EndY=0 EndZ=0
    g3: LineSegment StartX=0 StartY=0 StartZ=0 EndX=5 EndY=0 EndZ=0
  constraints (13):
    c: Vertical(g0)
    c: Distance(g0) = 1.5
    c: Horizontal(g1)
    c: Distance(g1) = 5
    c: Coincident(g1,g0)
    c: Vertical(g2)
    c: Distance(g2) = 1.5
    c: Coincident(g2,g1)
    c: Block(g1)
    c: Block(g2)
    c: Block(g0)
    c: Coincident(g3,g0)
    c: Coincident(g3,g2)
FEATURE [Part::Extrusion] Extrude027  label="solenoidDriverBottomLipTopExtrude017"
  Base = -> Sketch029
  Dir = (0,0.894389,-0.447291)
  DirMode = 2
  FaceMakerClass = Part::FaceMakerBullseye
  LengthFwd = -6.5
  LengthRev = 0
  Placement = pos=(0,-14.15,19.65) rot=(1,0,0;1.5708rad)
  Solid = true
  Symmetric = false
FEATURE [Sketcher::SketchObject] Sketch030
  FullyConstrained = true
  Placement = pos=(0,-14.3,2.37) rot=(-1,0,0;2.03453rad)
  sketch-geometry (4):
    g0: LineSegment StartX=0 StartY=1.5 StartZ=0 EndX=0 EndY=0 EndZ=0
    g1: LineSegment StartX=0 StartY=1.5 StartZ=0 EndX=5 EndY=1.5 EndZ=0
    g2: LineSegment StartX=5 StartY=1.5 StartZ=0 EndX=5 EndY=0 EndZ=0
    g3: LineSegment StartX=0 StartY=0 StartZ=0 EndX=5 EndY=0 EndZ=0
  constraints (13):
    c: Vertical(g0)
    c: Distance(g0) = 1.5
    c: Horizontal(g1)
    c: Distance(g1) = 5
    c: Coincident(g1,g0)
    c: Vertical(g2)
    c: Distance(g2) = 1.5
    c: Coincident(g2,g1)
    c: Block(g1)
    c: Block(g2)
    c: Block(g0)
    c: Coincident(g3,g0)
    c: Coincident(g3,g2)
FEATURE [Sketcher::SketchObject] Sketch031
  FullyConstrained = true
  Placement = pos=(0,-14.3,2.37) rot=(-1,0,0;2.03453rad)
  sketch-geometry (6):
    g0: LineSegment StartX=45.5 StartY=-21.2 StartZ=0 EndX=49.5 EndY=-21.2 EndZ=0
    g1: LineSegment StartX=45.5 StartY=0 StartZ=0 EndX=49.5 EndY=0 EndZ=0
    g2: LineSegment StartX=49.5 StartY=0 StartZ=0 EndX=49.5 EndY=-21.2 EndZ=0
    g3: LineSegment StartX=4 StartY=0 StartZ=0 EndX=4 EndY=-21.2 EndZ=0
    g4: LineSegment StartX=45.5 StartY=-21.2 StartZ=0 EndX=4 EndY=-21.2 EndZ=0
    g5: LineSegment StartX=4 StartY=0 StartZ=0 EndX=45.5 EndY=0 EndZ=0
  constraints (16):
    c: Horizontal(g0)
    c: Distance(g0) = 4
    c: Horizontal(g1)
    c: Distance(g1) = 4
    c: Coincident(g2,g1)
    c: Coincident(g2,g0)
    c: Vertical(g2)
    c: Block(g2)
    c: Vertical(g3)
    c: Coincident(g4,g0)
    c: Horizontal(g4)
    c: Coincident(g4,g3)
    c: Coincident(g5,g1)
    c: Horizontal(g5)
    c: Block(g3)
    c: Block(g5)
FEATURE [Part::Extrusion] Extrude028  label="removeFromSolenoidDriverMainExtrude021"
  Base = -> Sketch031
  Dir = (0,0.894389,-0.447291)
  DirMode = 2
  FaceMakerClass = Part::FaceMakerBullseye
  LengthFwd = 3.1
  LengthRev = 0
  Placement = pos=(-4,-2.42,-0.8) rot=(0,0,1;0rad)
  Solid = true
  Symmetric = false
FEATURE [Part::Extrusion] Extrude029  label="solenoidDriverBottomLipTopExtrude018"
  Base = -> Sketch030
  Dir = (0,0.894389,-0.447291)
  DirMode = 2
  FaceMakerClass = Part::FaceMakerBullseye
  LengthFwd = -6.5
  LengthRev = 0
  Placement = pos=(5,-14.15,19.65) rot=(1,0,0;1.5708rad)
  Solid = true
  Symmetric = false
FEATURE [Sketcher::SketchObject] Sketch032
  FullyConstrained = true
  Placement = pos=(0,-14.3,2.37) rot=(-1,0,0;2.03453rad)
  sketch-geometry (4):
    g0: LineSegment StartX=0 StartY=1.5 StartZ=0 EndX=0 EndY=0 EndZ=0
    g1: LineSegment StartX=0 StartY=1.5 StartZ=0 EndX=5 EndY=1.5 EndZ=0
    g2: LineSegment StartX=5 StartY=1.5 StartZ=0 EndX=5 EndY=0 EndZ=0
    g3: LineSegment StartX=0 StartY=0 StartZ=0 EndX=5 EndY=0 EndZ=0
  constraints (13):
    c: Vertical(g0)
    c: Distance(g0) = 1.5
    c: Horizontal(g1)
    c: Distance(g1) = 5
    c: Coincident(g1,g0)
    c: Vertical(g2)
    c: Distance(g2) = 1.5
    c: Coincident(g2,g1)
    c: Block(g1)
    c: Block(g2)
    c: Block(g0)
    c: Coincident(g3,g0)
    c: Coincident(g3,g2)
FEATURE [Part::Extrusion] Extrude030  label="solenoidDriverBottomLipTopExtrude019"
  Base = -> Sketch032
  Dir = (0,0.894389,-0.447291)
  DirMode = 2
  FaceMakerClass = Part::FaceMakerBullseye
  LengthFwd = -6.5
  LengthRev = 0
  Placement = pos=(0,-14.15,19.65) rot=(1,0,0;1.5708rad)
  Solid = true
  Symmetric = false
FEATURE [Part::MultiFuse] Fusion004
  Placement = pos=(0,1.4,2.65) rot=(0,0,1;0rad)
  Shapes = -> [Extrude029,Extrude030]
FEATURE [Part::MultiFuse] Fusion003
  Placement = pos=(-2.3,0,0) rot=(0,0,1;0rad)
  Shapes = -> [Extrude028,Fusion004]
FEATURE [Sketcher::SketchObject] Sketch033
  FullyConstrained = true
  Placement = pos=(0,-14.3,2.37) rot=(-1,0,0;2.03453rad)
  sketch-geometry (4):
    g0: LineSegment StartX=0 StartY=1.5 StartZ=0 EndX=0 EndY=0 EndZ=0
    g1: LineSegment StartX=0 StartY=1.5 StartZ=0 EndX=5 EndY=1.5 EndZ=0
    g2: LineSegment StartX=5 StartY=1.5 StartZ=0 EndX=5 EndY=0 EndZ=0
    g3: LineSegment StartX=0 StartY=0 StartZ=0 EndX=5 EndY=0 EndZ=0
  constraints (13):
    c: Vertical(g0)
    c: Distance(g0) = 1.5
    c: Horizontal(g1)
    c: Distance(g1) = 5
    c: Coincident(g1,g0)
    c: Vertical(g2)
    c: Distance(g2) = 1.5
    c: Coincident(g2,g1)
    c: Block(g1)
    c: Block(g2)
    c: Block(g0)
    c: Coincident(g3,g0)
    c: Coincident(g3,g2)
FEATURE [Sketcher::SketchObject] Sketch034
  FullyConstrained = true
  Placement = pos=(0,-14.3,2.37) rot=(-1,0,0;2.03453rad)
  sketch-geometry (4):
    g0: LineSegment StartX=0 StartY=1.5 StartZ=0 EndX=4 EndY=1.5 EndZ=0
    g1: LineSegment StartX=4 StartY=1.5 StartZ=0 EndX=4 EndY=-2.5 EndZ=0
    g2: LineSegment StartX=4 StartY=-2.5 StartZ=0 EndX=0 EndY=-2.5 EndZ=0
    g3: LineSegment StartX=0 StartY=1.5 StartZ=0 EndX=0 EndY=-2.5 EndZ=0
  constraints (11):
    c: Horizontal(g0)
    c: Distance(g0) = 4
    c: Block(g0)
    c: Coincident(g1,g0)
    c: Vertical(g1)
    c: Distance(g1) = 4
    c: Coincident(g2,g1)
    c: Horizontal(g2)
    c: Distance(g2) = 4
    c: Coincident(g3,g0)
    c: Coincident(g3,g2)
FEATURE [Part::Extrusion] Extrude020  label="removeFromSolenoidDriverMainExtrude020"
  Base = -> Sketch020
  Dir = (0,0.894389,-0.447291)
  DirMode = 2
  FaceMakerClass = Part::FaceMakerBullseye
  LengthFwd = 3.1
  LengthRev = 0
  Placement = pos=(-4,-2.42,-0.8) rot=(0,0,1;0rad)
  Solid = true
  Symmetric = false
FEATURE [Part::Fillet] Fillet
  Base = -> Fusion003
  Edges = 1 edges r=10: [Edge5]
  Placement = pos=(-2,0,0) rot=(0,0,1;0rad)
FEATURE [Part::MultiFuse] Fusion001
  Placement = pos=(0,1.4,2.65) rot=(0,0,1;0rad)
  Shapes = -> [Extrude026,Extrude027]
FEATURE [Part::MultiFuse] Fusion002
  Shapes = -> [Extrude020,Fusion001]
FEATURE [Sketcher::SketchObject] Sketch035
  FullyConstrained = true
  Placement = pos=(0,-14.3,2.37) rot=(-1,0,0;2.03453rad)
  sketch-geometry (4):
    g0: LineSegment StartX=0 StartY=1.5 StartZ=0 EndX=0 EndY=0 EndZ=0
    g1: LineSegment StartX=0 StartY=1.5 StartZ=0 EndX=5 EndY=1.5 EndZ=0
    g2: LineSegment StartX=5 StartY=1.5 StartZ=0 EndX=5 EndY=0 EndZ=0
    g3: LineSegment StartX=0 StartY=0 StartZ=0 EndX=5 EndY=0 EndZ=0
  constraints (13):
    c: Vertical(g0)
    c: Distance(g0) = 1.5
    c: Horizontal(g1)
    c: Distance(g1) = 5
    c: Coincident(g1,g0)
    c: Vertical(g2)
    c: Distance(g2) = 1.5
    c: Coincident(g2,g1)
    c: Block(g1)
    c: Block(g2)
    c: Block(g0)
    c: Coincident(g3,g0)
    c: Coincident(g3,g2)
FEATURE [Sketcher::SketchObject] Sketch036
  FullyConstrained = true
  Placement = pos=(0,-14.3,2.37) rot=(-1,0,0;2.03453rad)
  sketch-geometry (4):
    g0: LineSegment StartX=0 StartY=1.5 StartZ=0 EndX=0 EndY=0 EndZ=0
    g1: LineSegment StartX=0 StartY=1.5 StartZ=0 EndX=5 EndY=1.5 EndZ=0
    g2: LineSegment StartX=5 StartY=1.5 StartZ=0 EndX=5 EndY=0 EndZ=0
    g3: LineSegment StartX=0 StartY=0 StartZ=0 EndX=5 EndY=0 EndZ=0
  constraints (13):
    c: Vertical(g0)
    c: Distance(g0) = 1.5
    c: Horizontal(g1)
    c: Distance(g1) = 5
    c: Coincident(g1,g0)
    c: Vertical(g2)
    c: Distance(g2) = 1.5
    c: Coincident(g2,g1)
    c: Block(g1)
    c: Block(g2)
    c: Block(g0)
    c: Coincident(g3,g0)
    c: Coincident(g3,g2)
FEATURE [Part::Extrusion] Extrude031  label="solenoidDriverBottomLipTopExtrude020"
  Base = -> Sketch035
  Dir = (0,0.894389,-0.447291)
  DirMode = 2
  FaceMakerClass = Part::FaceMakerBullseye
  LengthFwd = -6.5
  LengthRev = 0
  Placement = pos=(5,-14.15,19.65) rot=(1,0,0;1.5708rad)
  Solid = true
  Symmetric = false
FEATURE [Part::Extrusion] Extrude032  label="solenoidDriverBottomLipTopExtrude021"
  Base = -> Sketch036
  Dir = (0,0.894389,-0.447291)
  DirMode = 2
  FaceMakerClass = Part::FaceMakerBullseye
  LengthFwd = -6.5
  LengthRev = 0
  Placement = pos=(0,-14.15,19.65) rot=(1,0,0;1.5708rad)
  Solid = true
  Symmetric = false
FEATURE [Part::MultiFuse] Fusion009
  Placement = pos=(8,1.4,2.65) rot=(0,0,1;0rad)
  Shapes = -> [Extrude031,Extrude032]
FEATURE [Part::MultiFuse] Fusion010  label="removeFromSolenoidDriver"
  Shapes = -> [Fusion009,Fillet,Fusion002]
FEATURE [Sketcher::SketchObject] Sketch037
  FullyConstrained = true
  Placement = pos=(0,0,0) rot=(1,0,0;1.5708rad)
  sketch-geometry (4):
    g0: Circle CenterX=64.05 CenterY=16.5 CenterZ=0 NormalX=0 NormalY=0 NormalZ=1 AngleXU=0 Radius=2.7
    g1: Circle CenterX=64.05 CenterY=8.5 CenterZ=0 NormalX=0 NormalY=0 NormalZ=1 AngleXU=0 Radius=2.7
    g2: Circle CenterX=84.15 CenterY=8.5 CenterZ=0 NormalX=0 NormalY=0 NormalZ=1 AngleXU=0 Radius=2.7
    g3: Circle CenterX=84.15 CenterY=16.5 CenterZ=0 NormalX=0 NormalY=0 NormalZ=1 AngleXU=0 Radius=2.7
  constraints (4):
    c: Block(g2)
    c: Block(g3)
    c: Block(g0)
    c: Block(g1)
FEATURE [Part::Extrusion] Extrude033  label="removeFromMainBodyToCreateScrewHoleCounterSinks001"
  Base = -> Sketch037
  Dir = (0,-1,1.1e-15)
  DirMode = 2
  FaceMakerClass = Part::FaceMakerBullseye
  LengthFwd = 1.9
  LengthRev = 0
  Placement = pos=(0.8,0,0) rot=(0,0,1;0rad)
  Solid = true
  Symmetric = false
FEATURE [Part::MultiFuse] Fusion011  label="removeFromMainBodyToCreateScrewHoleCounterSinks001Fusion011"
  Shapes = -> [Extrude014,Extrude033]
FEATURE [Sketcher::SketchObject] Sketch038
  FullyConstrained = true
  Placement = pos=(0,-14.3,2.37) rot=(-1,0,0;2.03453rad)
  sketch-geometry (4):
    g0: LineSegment StartX=33.9 StartY=-9.7 StartZ=0 EndX=33.9 EndY=-1.5 EndZ=0
    g1: LineSegment StartX=33.9 StartY=-1.5 StartZ=0 EndX=44.5 EndY=-1.5 EndZ=0
    g2: LineSegment StartX=33.9 StartY=-9.7 StartZ=0 EndX=44.5 EndY=-9.7 EndZ=0
    g3: LineSegment StartX=44.5 StartY=-1.5 StartZ=0 EndX=44.5 EndY=-9.7 EndZ=0
  constraints (10):
    c: Vertical(g0)
    c: Coincident(g1,g0)
    c: Horizontal(g1)
    c: Block(g1)
    c: Block(g0)
    c: Coincident(g2,g0)
    c: Horizontal(g2)
    c: Coincident(g3,g1)
    c: Coincident(g3,g2)
    c: Vertical(g3)
FEATURE [Part::Extrusion] Extrude034
  Base = -> Sketch038
  Dir = (0,0.894389,-0.447291)
  DirMode = 2
  FaceMakerClass = Part::FaceMakerBullseye
  LengthFwd = 16
  LengthRev = 0
  Placement = pos=(0,-22,7) rot=(0,0,1;0rad)
  Solid = true
  Symmetric = false
FEATURE [Sketcher::SketchObject] Sketch039
  FullyConstrained = true
  Placement = pos=(0,-14.3,2.37) rot=(-1,0,0;2.03453rad)
  sketch-geometry (4):
    g0: LineSegment StartX=5.5 StartY=-7.7 StartZ=0 EndX=13.3 EndY=-7.7 EndZ=0
    g1: LineSegment StartX=13.3 StartY=-7.7 StartZ=0 EndX=13.3 EndY=-13.1 EndZ=0
    g2: LineSegment StartX=13.3 StartY=-13.1 StartZ=0 EndX=5.5 EndY=-13.1 EndZ=0
    g3: LineSegment StartX=5.5 StartY=-7.7 StartZ=0 EndX=5.5 EndY=-13.1 EndZ=0
  constraints (12):
    c: Horizontal(g0)
    c: Distance(g0) = 7.8
    c: Coincident(g1,g0)
    c: Vertical(g1)
    c: Distance(g1) = 5.4
    c: Coincident(g2,g1)
    c: Horizontal(g2)
    c: Vertical(g3)
    c: Coincident(g3,g2)
    c: Block(g0)
    c: Block(g2)
    c: Block(g3)
FEATURE [Part::Extrusion] Extrude035  label="removeToMakeHoleForConnectorExtrude035"
  Base = -> Sketch039
  Dir = (0,0.894389,-0.447291)
  DirMode = 2
  FaceMakerClass = Part::FaceMakerBullseye
  LengthFwd = 15
  LengthRev = 0
  Placement = pos=(-4,-22,9.6469) rot=(0,0,1;0rad)
  Solid = true
  Symmetric = false
FEATURE [App::MeasureDistance] Distance  label="Distance: 4.00 mm"
  Distance = 4.00184
  P1 = (119.349,-15.3,8)
  P2 = (123.351,-15.3,8)
FEATURE [App::MeasureDistance] Distance001  label="Distance: 3.80 mm"
  Distance = 3.8
  P1 = (119.45,-15.3,8)
  P2 = (123.25,-15.3,8)
FEATURE [Part::Fillet] Fillet015
  Base = -> Extrude009
  Edges = 1 edges r=1.59: [Edge7]
FEATURE [Part::Fillet] Fillet016
  Base = -> Extrude017
  Edges = 1 edges r=1.49: [Edge12]
FEATURE [Part::Fillet] Fillet017
  Base = -> Fillet016
  Edges = 1 edges r=1.45: [Edge8]
FEATURE [Part::MultiFuse] Fusion012  label="main"
  Shapes = -> [Extrude,Revolve,Extrude005,Fillet003,Fillet012,Fillet014,Extrude025,Fusion,Fillet015,Fillet017]
FEATURE [Part::Cut] Cut001
  Base = -> Fusion012
  Tool = -> Box003
FEATURE [Part::Cut] Cut002
  Base = -> Cut001
  Tool = -> Box002
FEATURE [Part::Cut] Cut003
  Base = -> Cut002
  Tool = -> Cut
FEATURE [Part::Cut] Cut004
  Base = -> Cut003
  Tool = -> Extrude019
FEATURE [Part::Cut] Cut005
  Base = -> Cut004
  Tool = -> Fusion011
FEATURE [Part::Cut] Cut006
  Base = -> Cut005
  Tool = -> Extrude004
FEATURE [Part::Cut] Cut007
  Base = -> Cut006
  Tool = -> Extrude015
FEATURE [Part::Cut] Cut008
  Base = -> Cut007
  Tool = -> Extrude008
FEATURE [Part::Cut] Cut009
  Base = -> Cut008
  Tool = -> Fusion010
FEATURE [App::MeasureDistance] Distance002  label="Distance: 2.05 mm"
  Distance = 2.05453
  P1 = (1.5,-23.0732,21.402)
  P2 = (6e-15,-23,20)
FEATURE [Part::Cut] Cut010
  Base = -> Cut009
  Tool = -> Extrude035
FEATURE [Part::Cut] Cut011
  Base = -> Cut010
  Tool = -> Extrude034
FEATURE [Part::Box] Box004  label="Cube004"
  AttacherType = Attacher::AttachEngine3D
  Height = 10
  Length = 200
  Placement = pos=(-30,0,0) rot=(0,0,1;0rad)
  Width = 10
FEATURE [Part::Fillet] Fillet020
  Base = -> Box004
  Edges = 1 edges r=3.6: [Edge12]
FEATURE [Part::Box] Box005  label="Cube005"
  AttacherType = Attacher::AttachEngine3D
  Height = 10
  Length = 198
  Placement = pos=(-30,0,0) rot=(0,0,1;0rad)
  Width = 10
FEATURE [Part::Cut] Cut012
  Base = -> Box005
  Tool = -> Fillet020
FEATURE [Part::Box] Box006  label="Cube006"
  AttacherType = Attacher::AttachEngine3D
  Height = 5
  Length = 200
  Placement = pos=(-30,6.4,10) rot=(1,0,0;0rad)
  Width = 5
FEATURE [Part::Box] Box007  label="Cube007"
  AttacherType = Attacher::AttachEngine3D
  Height = 5
  Length = 200
  Placement = pos=(-30,6.4,10) rot=(1,0,0;0.872665rad)
  Width = 5
FEATURE [Part::MultiFuse] Fusion013  label="removeFromMainFusion013"
  Placement = pos=(0,-10,10) rot=(0,0,1;0rad)
  Shapes = -> [Box007,Box006,Cut012]
FEATURE [Mesh::Feature] v0_98_Cut013  label="v0_98-Cut013"
FEATURE [App::MeasureDistance] Distance003  label="Distance: 7.18 mm"
  Distance = 7.17719
  P1 = (117.773,-15.3145,-2.4)
  P2 = (124.951,-15.2973,-2.4)
FEATURE [Sketcher::SketchObject] Sketch040
  FullyConstrained = true
  Placement = pos=(0,-14.3,2.37) rot=(-1,0,0;2.03453rad)
  sketch-geometry (4):
    g0: LineSegment StartX=0 StartY=1.5 StartZ=0 EndX=0 EndY=0 EndZ=0
    g1: LineSegment StartX=0 StartY=1.5 StartZ=0 EndX=5 EndY=1.5 EndZ=0
    g2: LineSegment StartX=5 StartY=1.5 StartZ=0 EndX=5 EndY=0 EndZ=0
    g3: LineSegment StartX=0 StartY=0 StartZ=0 EndX=5 EndY=0 EndZ=0
  constraints (13):
    c: Vertical(g0)
    c: Distance(g0) = 1.5
    c: Horizontal(g1)
    c: Distance(g1) = 5
    c: Coincident(g1,g0)
    c: Vertical(g2)
    c: Distance(g2) = 1.5
    c: Coincident(g2,g1)
    c: Block(g1)
    c: Block(g2)
    c: Block(g0)
    c: Coincident(g3,g0)
    c: Coincident(g3,g2)
FEATURE [Part::Extrusion] Extrude036
  Base = -> Sketch040
  Dir = (0,0.894389,-0.447291)
  DirMode = 2
  FaceMakerClass = Part::FaceMakerBullseye
  LengthFwd = 1.4
  LengthRev = 0
  Placement = pos=(0,8.25,17.58) rot=(0,0,1;0rad)
  Solid = true
  Symmetric = false
FEATURE [Sketcher::SketchObject] Sketch041
  FullyConstrained = true
  Placement = pos=(0,-14.3,2.37) rot=(-1,0,0;2.03453rad)
  sketch-geometry (4):
    g0: LineSegment StartX=0 StartY=1.5 StartZ=0 EndX=0 EndY=0 EndZ=0
    g1: LineSegment StartX=0 StartY=1.5 StartZ=0 EndX=5 EndY=1.5 EndZ=0
    g2: LineSegment StartX=5 StartY=1.5 StartZ=0 EndX=5 EndY=0 EndZ=0
    g3: LineSegment StartX=0 StartY=0 StartZ=0 EndX=5 EndY=0 EndZ=0
  constraints (13):
    c: Vertical(g0)
    c: Distance(g0) = 1.5
    c: Horizontal(g1)
    c: Distance(g1) = 5
    c: Coincident(g1,g0)
    c: Vertical(g2)
    c: Distance(g2) = 1.5
    c: Coincident(g2,g1)
    c: Block(g1)
    c: Block(g2)
    c: Block(g0)
    c: Coincident(g3,g0)
    c: Coincident(g3,g2)
FEATURE [Part::Extrusion] Extrude037
  Base = -> Sketch041
  Dir = (0,0.894389,-0.447291)
  DirMode = 2
  FaceMakerClass = Part::FaceMakerBullseye
  LengthFwd = 1.4
  LengthRev = 0
  Placement = pos=(0,6.11,13.33) rot=(0,0,1;0rad)
  Solid = true
  Symmetric = false
FEATURE [Part::MultiFuse] Fusion014  label="screwSpacerFusion014"
  Shapes = -> [Extrude037,Extrude036]
FEATURE [Sketcher::SketchObject] Sketch042
  FullyConstrained = true
  Placement = pos=(0,-14.3,2.37) rot=(-1,0,0;2.03453rad)
  sketch-geometry (4):
    g0: LineSegment StartX=0 StartY=1.5 StartZ=0 EndX=0 EndY=0 EndZ=0
    g1: LineSegment StartX=0 StartY=1.5 StartZ=0 EndX=5 EndY=1.5 EndZ=0
    g2: LineSegment StartX=5 StartY=1.5 StartZ=0 EndX=5 EndY=0 EndZ=0
    g3: LineSegment StartX=0 StartY=0 StartZ=0 EndX=5 EndY=0 EndZ=0
  constraints (13):
    c: Vertical(g0)
    c: Distance(g0) = 1.5
    c: Horizontal(g1)
    c: Distance(g1) = 5
    c: Coincident(g1,g0)
    c: Vertical(g2)
    c: Distance(g2) = 1.5
    c: Coincident(g2,g1)
    c: Block(g1)
    c: Block(g2)
    c: Block(g0)
    c: Coincident(g3,g0)
    c: Coincident(g3,g2)
FEATURE [Part::Extrusion] Extrude038
  Base = -> Sketch042
  Dir = (0,0.894389,-0.447291)
  DirMode = 2
  FaceMakerClass = Part::FaceMakerBullseye
  LengthFwd = 1.4
  LengthRev = 0
  Placement = pos=(0,8.459,18) rot=(0,0,1;0rad)
  Solid = true
  Symmetric = false
FEATURE [Part::MultiFuse] Fusion015  label="screwSpacerFusion014Fusion015"
  Placement = pos=(0,0.35,-0.18) rot=(0,0,1;0rad)
  Shapes = -> [Extrude038,Fusion014]
FEATURE [Part::Cylinder] Cylinder
  Angle = 360
  AttacherType = Attacher::AttachEngine3D
  Height = 10
  Placement = pos=(0,10,0) rot=(0,0,1;0rad)
  Radius = 1.5
FEATURE [Part::Cylinder] Cylinder001
  Angle = 360
  AttacherType = Attacher::AttachEngine3D
  Height = 10
  Placement = pos=(3,10,0) rot=(0,0,1;0rad)
  Radius = 1.5
FEATURE [Part::Box] Box008  label="Cube008"
  AttacherType = Attacher::AttachEngine3D
  Height = 10
  Length = 3
  Placement = pos=(0,8.5,0) rot=(0,0,1;0rad)
  Width = 3
FEATURE [Part::MultiFuse] Fusion016  label="holeForWireFusion016"
  Shapes = -> [Cylinder001,Box008,Cylinder]
FEATURE [Part::Box] Box009  label="Cube009"
  AttacherType = Attacher::AttachEngine3D
  Height = 10
  Length = 3
  Placement = pos=(0,8.5,0) rot=(0,0,1;0rad)
  Width = 3
FEATURE [Part::Cylinder] Cylinder002
  Angle = 360
  AttacherType = Attacher::AttachEngine3D
  Height = 10
  Placement = pos=(0,10,0) rot=(0,0,1;0rad)
  Radius = 1.5
FEATURE [Part::Cylinder] Cylinder003
  Angle = 360
  AttacherType = Attacher::AttachEngine3D
  Height = 10
  Placement = pos=(3,10,0) rot=(0,0,1;0rad)
  Radius = 1.5
FEATURE [Part::MultiFuse] Fusion017  label="holeForWireFusion017"
  Placement = pos=(0,0,10) rot=(0,0,1;0rad)
  Shapes = -> [Cylinder003,Box009,Cylinder002]
FEATURE [Part::MultiFuse] Fusion018  label="holeForWireFusion018"
  Placement = pos=(0,0,0) rot=(0,1,0;-1.5708rad)
  Shapes = -> [Fusion017,Fusion016]
FEATURE [Part::Box] Box010  label="Cube010"
  AttacherType = Attacher::AttachEngine3D
  Height = 0.1
  Length = 0.1
  Placement = pos=(-2,10,0) rot=(0,0.995037,0.099504;0rad)
  Width = 0.1
FEATURE [Part::MultiFuse] Fusion019
  Placement = pos=(0,10,0) rot=(1,0,0;1.5708rad)
  Shapes = -> [Box010,Fusion018]
FEATURE [Part::Box] Box011  label="Cube011"
  AttacherType = Attacher::AttachEngine3D
  Height = 0.1
  Length = 1.1
  Placement = pos=(-2,10,10) rot=(0,0.995037,0.099504;0rad)
  Width = 0.1
FEATURE [Part::MultiFuse] Fusion020
  Placement = pos=(0,0,0) rot=(0,1,0;0.349066rad)
  Shapes = -> [Box011,Fusion019]
FEATURE [Part::Box] Box012  label="Cube012"
  AttacherType = Attacher::AttachEngine3D
  Height = 0.1
  Length = 1.1
  Placement = pos=(-2,10,10) rot=(0,0.995037,0.099504;0rad)
  Width = 0.1
FEATURE [Part::MultiFuse] Fusion021
  Placement = pos=(0,30,0) rot=(0,0,1;-2.6529rad)
  Shapes = -> [Box012,Fusion020]
FEATURE [Part::Box] Box013  label="Cube013"
  AttacherType = Attacher::AttachEngine3D
  Height = 0.1
  Length = 1.1
  Placement = pos=(2,19,10) rot=(0,0.995037,0.099504;0rad)
  Width = 0.1
FEATURE [Part::MultiFuse] Fusion022  label="holeForWire"
  Placement = pos=(15,-49.8,-8.2) rot=(0,0,1;0rad)
  Shapes = -> [Box013,Fusion021]
FEATURE [Part::Cut] Cut013
  Base = -> Cut011
  Tool = -> Fusion013
FEATURE [Part::Cut] Cut014
  Base = -> Cut013
  Tool = -> Fusion022
FEATURE [Sketcher::SketchObject] Sketch043
  FullyConstrained = true
  MapMode = 4
  Placement = pos=(0,0,0) rot=(0.57735,0.57735,0.57735;2.0944rad)
  Support = -> [Cut014]
  sketch-geometry (14):
    g0: LineSegment StartX=6.08745 StartY=-4.11588 StartZ=0 EndX=6.08745 EndY=-2.11589 EndZ=0
    g1: LineSegment StartX=3.58745 StartY=2.38411 StartZ=0 EndX=3.58745 EndY=4.38411 EndZ=0
    g2: LineSegment StartX=8.08745 StartY=1.38411 StartZ=0 EndX=8.08745 EndY=-1.11589 EndZ=0
    g3: ArcOfCircle CenterX=7.08745 CenterY=-1.11589 CenterZ=0 NormalX=0 NormalY=0 NormalZ=1 AngleXU=0 Radius=1 StartAngle=4.71239 EndAngle=6.28319
    g4: LineSegment StartX=6.08745 StartY=-2.11589 StartZ=0 EndX=7.08745 EndY=-2.11589 EndZ=0
    g5: LineSegment StartX=6.08745 StartY=-4.11588 StartZ=0 EndX=7.08745 EndY=-4.11588 EndZ=0
    g6: ArcOfCircle CenterX=7.08745 CenterY=-1.11589 CenterZ=0 NormalX=0 NormalY=0 NormalZ=1 AngleXU=0 Radius=3 StartAngle=4.71239 EndAngle=6.28319
    g7: ArcOfCircle CenterX=7.08745 CenterY=1.38411 CenterZ=0 NormalX=0 NormalY=0 NormalZ=1 AngleXU=0 Radius=1 StartAngle=5.35e-14 EndAngle=1.5708
    g8: LineSegment StartX=3.58745 StartY=4.38411 StartZ=0 EndX=7.08745 EndY=4.38411 EndZ=0
    g9: LineSegment StartX=10.0875 StartY=-1.11588 StartZ=0 EndX=10.0875 EndY=1.38411 EndZ=0
    g10: ArcOfCircle CenterX=7.08745 CenterY=1.38411 CenterZ=0 NormalX=0 NormalY=0 NormalZ=1 AngleXU=0 Radius=3 StartAngle=3.57e-14 EndAngle=1.5708
    g11: LineSegment StartX=3.58745 StartY=2.38411 StartZ=0 EndX=3.58745 EndY=1.38411 EndZ=0
    g12: ArcOfCircle CenterX=4.58745 CenterY=1.38412 CenterZ=0 NormalX=0 NormalY=0 NormalZ=1 AngleXU=0 Radius=1 StartAngle=1.57081 EndAngle=3.14159
    g13: LineSegment StartX=4.58744 StartY=2.38411 StartZ=0 EndX=7.08745 EndY=2.38411 EndZ=0
  constraints (33):
    c: Vertical(g0)
    c: Vertical(g1)
    c: Distance(g1) = 2
    c: Block(g0)
    c: Block(g2)
    c: Coincident(g3,g2)
    c: Coincident(g4,g0)
    c: Coincident(g4,g3)
    c: Horizontal(g4)
    c: Block(g3)
    c: Coincident(g5,g0)
    c: Horizontal(g5)
    c: Coincident(g6,g3)
    c: Block(g6)
    c: Block(g5)
    c: Coincident(g7,g2)
    c: Block(g7)
    c: Coincident(g8,g1)
    c: Coincident(g9,g6)
    c: Vertical(g9)
    c: Coincident(g10,g7)
    c: Block(g10)
    c: Block(g8)
    c: Block(g9)
    c: Coincident(g11,g1)
    c: Vertical(g11)
    c: Distance(g11) = 1
    c: Coincident(g12,g11)
    c: Coincident(g13,g12)
    c: Coincident(g13,g7)
    c: Horizontal(g13)
    c: Block(g13)
    c: Block(g12)
FEATURE [Sketcher::SketchObject] Sketch044
  FullyConstrained = true
  MapMode = 4
  Placement = pos=(0,0,0) rot=(0.57735,0.57735,0.57735;2.0944rad)
  Support = -> [Cut014]
  sketch-geometry (14):
    g0: LineSegment StartX=6.08745 StartY=-4.11588 StartZ=0 EndX=6.08745 EndY=-2.11589 EndZ=0
    g1: LineSegment StartX=8.08745 StartY=1.38411 StartZ=0 EndX=8.08745 EndY=-1.11589 EndZ=0
    g2: ArcOfCircle CenterX=7.08745 CenterY=-1.11589 CenterZ=0 NormalX=0 NormalY=0 NormalZ=1 AngleXU=0 Radius=1 StartAngle=4.71239 EndAngle=6.28319
    g3: LineSegment StartX=6.08745 StartY=-2.11589 StartZ=0 EndX=7.08745 EndY=-2.11589 EndZ=0
    g4: LineSegment StartX=6.08745 StartY=-4.11588 StartZ=0 EndX=7.08745 EndY=-4.11588 EndZ=0
    g5: ArcOfCircle CenterX=7.08745 CenterY=-1.11589 CenterZ=0 NormalX=0 NormalY=0 NormalZ=1 AngleXU=0 Radius=3 StartAngle=4.71239 EndAngle=6.28319
    g6: ArcOfCircle CenterX=7.08745 CenterY=1.38411 CenterZ=0 NormalX=0 NormalY=0 NormalZ=1 AngleXU=0 Radius=1 StartAngle=5.35e-14 EndAngle=1.5708
    g7: LineSegment StartX=10.0875 StartY=-1.11588 StartZ=0 EndX=10.0875 EndY=1.38411 EndZ=0
    g8: ArcOfCircle CenterX=7.08745 CenterY=1.38411 CenterZ=0 NormalX=0 NormalY=0 NormalZ=1 AngleXU=0 Radius=3 StartAngle=3.57e-14 EndAngle=1.5708
    g9: ArcOfCircle CenterX=4.58745 CenterY=1.38412 CenterZ=0 NormalX=0 NormalY=0 NormalZ=1 AngleXU=0 Radius=1 StartAngle=1.57081 EndAngle=3.14159
    g10: LineSegment StartX=4.58744 StartY=2.38411 StartZ=0 EndX=7.08745 EndY=2.38411 EndZ=0
    g11: LineSegment StartX=4.58745 StartY=4.38411 StartZ=0 EndX=7.08745 EndY=4.38411 EndZ=0
    g12: ArcOfCircle CenterX=4.58745 CenterY=5.38411 CenterZ=0 NormalX=0 NormalY=0 NormalZ=1 AngleXU=0 Radius=1 StartAngle=3.14159 EndAngle=4.71239
    g13: LineSegment StartX=3.58745 StartY=5.38411 StartZ=0 EndX=3.58745 EndY=1.38411 EndZ=0
  constraints (33):
    c: Vertical(g0)
    c: Block(g0)
    c: Block(g1)
    c: Coincident(g2,g1)
    c: Coincident(g3,g0)
    c: Coincident(g3,g2)
    c: Horizontal(g3)
    c: Block(g2)
    c: Coincident(g4,g0)
    c: Horizontal(g4)
    c: Coincident(g5,g2)
    c: Block(g5)
    c: Block(g4)
    c: Coincident(g6,g1)
    c: Block(g6)
    c: Coincident(g7,g5)
    c: Vertical(g7)
    c: Coincident(g8,g6)
    c: Block(g8)
    c: Block(g7)
    c: Coincident(g10,g9)
    c: Coincident(g10,g6)
    c: Horizontal(g10)
    c: Block(g10)
    c: Block(g9)
    c: Coincident(g11,g8)
    c: Horizontal(g11)
    c: Block(g12)
    c: Block(g11)
    c: Coincident(g13,g12)
    c: Coincident(g13,g9)
    c: Vertical(g13)
    c: Tangent(g13,g9)
FEATURE [Part::Extrusion] Extrude039
  Base = -> Sketch044
  Dir = (1,0,0)
  DirMode = 2
  FaceMakerClass = Part::FaceMakerBullseye
  LengthFwd = 10
  LengthRev = 0
  Placement = pos=(8,-22.615,4.115) rot=(0,0,1;3.14159rad)
  Solid = true
  Symmetric = false
FEATURE [App::MeasureDistance] Distance004  label="Distance: 42.16 mm"
  Distance = 42.1607
  P1 = (14.6786,-26.2,1.24491)
  P2 = (-27.4815,-26.2,1.03853)
FEATURE [Sketcher::SketchObject] Sketch045
  FullyConstrained = true
  MapMode = 4
  Placement = pos=(0,0,0) rot=(0.57735,0.57735,0.57735;2.0944rad)
  Support = -> [Cut014]
  sketch-geometry (14):
    g0: LineSegment StartX=6.08745 StartY=-4.11588 StartZ=0 EndX=6.08745 EndY=-2.11589 EndZ=0
    g1: LineSegment StartX=8.08745 StartY=1.38411 StartZ=0 EndX=8.08745 EndY=-1.11589 EndZ=0
    g2: ArcOfCircle CenterX=7.08745 CenterY=-1.11589 CenterZ=0 NormalX=0 NormalY=0 NormalZ=1 AngleXU=0 Radius=1 StartAngle=4.71239 EndAngle=6.28319
    g3: LineSegment StartX=6.08745 StartY=-2.11589 StartZ=0 EndX=7.08745 EndY=-2.11589 EndZ=0
    g4: LineSegment StartX=6.08745 StartY=-4.11588 StartZ=0 EndX=7.08745 EndY=-4.11588 EndZ=0
    g5: ArcOfCircle CenterX=7.08745 CenterY=-1.11589 CenterZ=0 NormalX=0 NormalY=0 NormalZ=1 AngleXU=0 Radius=3 StartAngle=4.71239 EndAngle=6.28319
    g6: ArcOfCircle CenterX=7.08745 CenterY=1.38411 CenterZ=0 NormalX=0 NormalY=0 NormalZ=1 AngleXU=0 Radius=1 StartAngle=5.35e-14 EndAngle=1.5708
    g7: LineSegment StartX=10.0875 StartY=-1.11588 StartZ=0 EndX=10.0875 EndY=1.38411 EndZ=0
    g8: ArcOfCircle CenterX=7.08745 CenterY=1.38411 CenterZ=0 NormalX=0 NormalY=0 NormalZ=1 AngleXU=0 Radius=3 StartAngle=3.57e-14 EndAngle=1.5708
    g9: ArcOfCircle CenterX=4.58745 CenterY=1.38412 CenterZ=0 NormalX=0 NormalY=0 NormalZ=1 AngleXU=0 Radius=1 StartAngle=1.57081 EndAngle=3.14159
    g10: LineSegment StartX=4.58744 StartY=2.38411 StartZ=0 EndX=7.08745 EndY=2.38411 EndZ=0
    g11: LineSegment StartX=4.58745 StartY=4.38411 StartZ=0 EndX=7.08745 EndY=4.38411 EndZ=0
    g12: ArcOfCircle CenterX=4.58745 CenterY=5.38411 CenterZ=0 NormalX=0 NormalY=0 NormalZ=1 AngleXU=0 Radius=1 StartAngle=3.14159 EndAngle=4.71239
    g13: LineSegment StartX=3.58745 StartY=5.38411 StartZ=0 EndX=3.58745 EndY=1.38411 EndZ=0
  constraints (33):
    c: Vertical(g0)
    c: Block(g0)
    c: Block(g1)
    c: Coincident(g2,g1)
    c: Coincident(g3,g0)
    c: Coincident(g3,g2)
    c: Horizontal(g3)
    c: Block(g2)
    c: Coincident(g4,g0)
    c: Horizontal(g4)
    c: Coincident(g5,g2)
    c: Block(g5)
    c: Block(g4)
    c: Coincident(g6,g1)
    c: Block(g6)
    c: Coincident(g7,g5)
    c: Vertical(g7)
    c: Coincident(g8,g6)
    c: Block(g8)
    c: Block(g7)
    c: Coincident(g10,g9)
    c: Coincident(g10,g6)
    c: Horizontal(g10)
    c: Block(g10)
    c: Block(g9)
    c: Coincident(g11,g8)
    c: Horizontal(g11)
    c: Block(g12)
    c: Block(g11)
    c: Coincident(g13,g12)
    c: Coincident(g13,g9)
    c: Vertical(g13)
    c: Tangent(g13,g9)
FEATURE [Part::Extrusion] Extrude040
  Base = -> Sketch045
  Dir = (1,0,0)
  DirMode = 2
  FaceMakerClass = Part::FaceMakerBullseye
  LengthFwd = 10
  LengthRev = 0
  Placement = pos=(-17.5,-22.615,4.115) rot=(0,0,1;3.14159rad)
  Solid = true
  Symmetric = false
FEATURE [Sketcher::SketchObject] Sketch046
  FullyConstrained = true
  MapMode = 4
  Placement = pos=(0,0,0) rot=(0.57735,0.57735,0.57735;2.0944rad)
  Support = -> [Cut014]
  sketch-geometry (14):
    g0: LineSegment StartX=6.08745 StartY=-4.11588 StartZ=0 EndX=6.08745 EndY=-2.11589 EndZ=0
    g1: LineSegment StartX=8.08745 StartY=1.38411 StartZ=0 EndX=8.08745 EndY=-1.11589 EndZ=0
    g2: ArcOfCircle CenterX=7.08745 CenterY=-1.11589 CenterZ=0 NormalX=0 NormalY=0 NormalZ=1 AngleXU=0 Radius=1 StartAngle=4.71239 EndAngle=6.28319
    g3: LineSegment StartX=6.08745 StartY=-2.11589 StartZ=0 EndX=7.08745 EndY=-2.11589 EndZ=0
    g4: LineSegment StartX=6.08745 StartY=-4.11588 StartZ=0 EndX=7.08745 EndY=-4.11588 EndZ=0
    g5: ArcOfCircle CenterX=7.08745 CenterY=-1.11589 CenterZ=0 NormalX=0 NormalY=0 NormalZ=1 AngleXU=0 Radius=3 StartAngle=4.71239 EndAngle=6.28319
    g6: ArcOfCircle CenterX=7.08745 CenterY=1.38411 CenterZ=0 NormalX=0 NormalY=0 NormalZ=1 AngleXU=0 Radius=1 StartAngle=5.35e-14 EndAngle=1.5708
    g7: LineSegment StartX=10.0875 StartY=-1.11588 StartZ=0 EndX=10.0875 EndY=1.38411 EndZ=0
    g8: ArcOfCircle CenterX=7.08745 CenterY=1.38411 CenterZ=0 NormalX=0 NormalY=0 NormalZ=1 AngleXU=0 Radius=3 StartAngle=3.57e-14 EndAngle=1.5708
    g9: ArcOfCircle CenterX=4.58745 CenterY=1.38412 CenterZ=0 NormalX=0 NormalY=0 NormalZ=1 AngleXU=0 Radius=1 StartAngle=1.57081 EndAngle=3.14159
    g10: LineSegment StartX=4.58744 StartY=2.38411 StartZ=0 EndX=7.08745 EndY=2.38411 EndZ=0
    g11: LineSegment StartX=4.58745 StartY=4.38411 StartZ=0 EndX=7.08745 EndY=4.38411 EndZ=0
    g12: ArcOfCircle CenterX=4.58745 CenterY=5.38411 CenterZ=0 NormalX=0 NormalY=0 NormalZ=1 AngleXU=0 Radius=1 StartAngle=3.14159 EndAngle=4.71239
    g13: LineSegment StartX=3.58745 StartY=5.38411 StartZ=0 EndX=3.58745 EndY=1.38411 EndZ=0
  constraints (33):
    c: Vertical(g0)
    c: Block(g0)
    c: Block(g1)
    c: Coincident(g2,g1)
    c: Coincident(g3,g0)
    c: Coincident(g3,g2)
    c: Horizontal(g3)
    c: Block(g2)
    c: Coincident(g4,g0)
    c: Horizontal(g4)
    c: Coincident(g5,g2)
    c: Block(g5)
    c: Block(g4)
    c: Coincident(g6,g1)
    c: Block(g6)
    c: Coincident(g7,g5)
    c: Vertical(g7)
    c: Coincident(g8,g6)
    c: Block(g8)
    c: Block(g7)
    c: Coincident(g10,g9)
    c: Coincident(g10,g6)
    c: Horizontal(g10)
    c: Block(g10)
    c: Block(g9)
    c: Coincident(g11,g8)
    c: Horizontal(g11)
    c: Block(g12)
    c: Block(g11)
    c: Coincident(g13,g12)
    c: Coincident(g13,g9)
    c: Vertical(g13)
    c: Tangent(g13,g9)
FEATURE [Sketcher::SketchObject] Sketch047
  FullyConstrained = true
  MapMode = 4
  Placement = pos=(0,0,0) rot=(0.57735,0.57735,0.57735;2.0944rad)
  Support = -> [Cut014]
  sketch-geometry (14):
    g0: LineSegment StartX=6.08745 StartY=-4.11588 StartZ=0 EndX=6.08745 EndY=-2.11589 EndZ=0
    g1: LineSegment StartX=8.08745 StartY=1.38411 StartZ=0 EndX=8.08745 EndY=-1.11589 EndZ=0
    g2: ArcOfCircle CenterX=7.08745 CenterY=-1.11589 CenterZ=0 NormalX=0 NormalY=0 NormalZ=1 AngleXU=0 Radius=1 StartAngle=4.71239 EndAngle=6.28319
    g3: LineSegment StartX=6.08745 StartY=-2.11589 StartZ=0 EndX=7.08745 EndY=-2.11589 EndZ=0
    g4: LineSegment StartX=6.08745 StartY=-4.11588 StartZ=0 EndX=7.08745 EndY=-4.11588 EndZ=0
    g5: ArcOfCircle CenterX=7.08745 CenterY=-1.11589 CenterZ=0 NormalX=0 NormalY=0 NormalZ=1 AngleXU=0 Radius=3 StartAngle=4.71239 EndAngle=6.28319
    g6: ArcOfCircle CenterX=7.08745 CenterY=1.38411 CenterZ=0 NormalX=0 NormalY=0 NormalZ=1 AngleXU=0 Radius=1 StartAngle=5.35e-14 EndAngle=1.5708
    g7: LineSegment StartX=10.0875 StartY=-1.11588 StartZ=0 EndX=10.0875 EndY=1.38411 EndZ=0
    g8: ArcOfCircle CenterX=7.08745 CenterY=1.38411 CenterZ=0 NormalX=0 NormalY=0 NormalZ=1 AngleXU=0 Radius=3 StartAngle=3.57e-14 EndAngle=1.5708
    g9: ArcOfCircle CenterX=4.58745 CenterY=1.38412 CenterZ=0 NormalX=0 NormalY=0 NormalZ=1 AngleXU=0 Radius=1 StartAngle=1.57081 EndAngle=3.14159
    g10: LineSegment StartX=4.58744 StartY=2.38411 StartZ=0 EndX=7.08745 EndY=2.38411 EndZ=0
    g11: LineSegment StartX=4.58745 StartY=4.38411 StartZ=0 EndX=7.08745 EndY=4.38411 EndZ=0
    g12: ArcOfCircle CenterX=4.58745 CenterY=5.38411 CenterZ=0 NormalX=0 NormalY=0 NormalZ=1 AngleXU=0 Radius=1 StartAngle=3.14159 EndAngle=4.71239
    g13: LineSegment StartX=3.58745 StartY=5.38411 StartZ=0 EndX=3.58745 EndY=1.38411 EndZ=0
  constraints (33):
    c: Vertical(g0)
    c: Block(g0)
    c: Block(g1)
    c: Coincident(g2,g1)
    c: Coincident(g3,g0)
    c: Coincident(g3,g2)
    c: Horizontal(g3)
    c: Block(g2)
    c: Coincident(g4,g0)
    c: Horizontal(g4)
    c: Coincident(g5,g2)
    c: Block(g5)
    c: Block(g4)
    c: Coincident(g6,g1)
    c: Block(g6)
    c: Coincident(g7,g5)
    c: Vertical(g7)
    c: Coincident(g8,g6)
    c: Block(g8)
    c: Block(g7)
    c: Coincident(g10,g9)
    c: Coincident(g10,g6)
    c: Horizontal(g10)
    c: Block(g10)
    c: Block(g9)
    c: Coincident(g11,g8)
    c: Horizontal(g11)
    c: Block(g12)
    c: Block(g11)
    c: Coincident(g13,g12)
    c: Coincident(g13,g9)
    c: Vertical(g13)
    c: Tangent(g13,g9)
FEATURE [Sketcher::SketchObject] Sketch048
  FullyConstrained = true
  MapMode = 4
  Placement = pos=(0,0,0) rot=(0.57735,0.57735,0.57735;2.0944rad)
  Support = -> [Cut014]
  sketch-geometry (14):
    g0: LineSegment StartX=6.08745 StartY=-4.11588 StartZ=0 EndX=6.08745 EndY=-2.11589 EndZ=0
    g1: LineSegment StartX=8.08745 StartY=1.38411 StartZ=0 EndX=8.08745 EndY=-1.11589 EndZ=0
    g2: ArcOfCircle CenterX=7.08745 CenterY=-1.11589 CenterZ=0 NormalX=0 NormalY=0 NormalZ=1 AngleXU=0 Radius=1 StartAngle=4.71239 EndAngle=6.28319
    g3: LineSegment StartX=6.08745 StartY=-2.11589 StartZ=0 EndX=7.08745 EndY=-2.11589 EndZ=0
    g4: LineSegment StartX=6.08745 StartY=-4.11588 StartZ=0 EndX=7.08745 EndY=-4.11588 EndZ=0
    g5: ArcOfCircle CenterX=7.08745 CenterY=-1.11589 CenterZ=0 NormalX=0 NormalY=0 NormalZ=1 AngleXU=0 Radius=3 StartAngle=4.71239 EndAngle=6.28319
    g6: ArcOfCircle CenterX=7.08745 CenterY=1.38411 CenterZ=0 NormalX=0 NormalY=0 NormalZ=1 AngleXU=0 Radius=1 StartAngle=5.35e-14 EndAngle=1.5708
    g7: LineSegment StartX=10.0875 StartY=-1.11588 StartZ=0 EndX=10.0875 EndY=1.38411 EndZ=0
    g8: ArcOfCircle CenterX=7.08745 CenterY=1.38411 CenterZ=0 NormalX=0 NormalY=0 NormalZ=1 AngleXU=0 Radius=3 StartAngle=3.57e-14 EndAngle=1.5708
    g9: ArcOfCircle CenterX=4.58745 CenterY=1.38412 CenterZ=0 NormalX=0 NormalY=0 NormalZ=1 AngleXU=0 Radius=1 StartAngle=1.57081 EndAngle=3.14159
    g10: LineSegment StartX=4.58744 StartY=2.38411 StartZ=0 EndX=7.08745 EndY=2.38411 EndZ=0
    g11: LineSegment StartX=4.58745 StartY=4.38411 StartZ=0 EndX=7.08745 EndY=4.38411 EndZ=0
    g12: ArcOfCircle CenterX=4.58745 CenterY=5.38411 CenterZ=0 NormalX=0 NormalY=0 NormalZ=1 AngleXU=0 Radius=1 StartAngle=3.14159 EndAngle=4.71239
    g13: LineSegment StartX=3.58745 StartY=5.38411 StartZ=0 EndX=3.58745 EndY=1.38411 EndZ=0
  constraints (33):
    c: Vertical(g0)
    c: Block(g0)
    c: Block(g1)
    c: Coincident(g2,g1)
    c: Coincident(g3,g0)
    c: Coincident(g3,g2)
    c: Horizontal(g3)
    c: Block(g2)
    c: Coincident(g4,g0)
    c: Horizontal(g4)
    c: Coincident(g5,g2)
    c: Block(g5)
    c: Block(g4)
    c: Coincident(g6,g1)
    c: Block(g6)
    c: Coincident(g7,g5)
    c: Vertical(g7)
    c: Coincident(g8,g6)
    c: Block(g8)
    c: Block(g7)
    c: Coincident(g10,g9)
    c: Coincident(g10,g6)
    c: Horizontal(g10)
    c: Block(g10)
    c: Block(g9)
    c: Coincident(g11,g8)
    c: Horizontal(g11)
    c: Block(g12)
    c: Block(g11)
    c: Coincident(g13,g12)
    c: Coincident(g13,g9)
    c: Vertical(g13)
    c: Tangent(g13,g9)
FEATURE [Sketcher::SketchObject] Sketch049
  FullyConstrained = true
  MapMode = 4
  Placement = pos=(0,0,0) rot=(0.57735,0.57735,0.57735;2.0944rad)
  Support = -> [Cut014]
  sketch-geometry (14):
    g0: LineSegment StartX=6.08745 StartY=-4.11588 StartZ=0 EndX=6.08745 EndY=-2.11589 EndZ=0
    g1: LineSegment StartX=8.08745 StartY=1.38411 StartZ=0 EndX=8.08745 EndY=-1.11589 EndZ=0
    g2: ArcOfCircle CenterX=7.08745 CenterY=-1.11589 CenterZ=0 NormalX=0 NormalY=0 NormalZ=1 AngleXU=0 Radius=1 StartAngle=4.71239 EndAngle=6.28319
    g3: LineSegment StartX=6.08745 StartY=-2.11589 StartZ=0 EndX=7.08745 EndY=-2.11589 EndZ=0
    g4: LineSegment StartX=6.08745 StartY=-4.11588 StartZ=0 EndX=7.08745 EndY=-4.11588 EndZ=0
    g5: ArcOfCircle CenterX=7.08745 CenterY=-1.11589 CenterZ=0 NormalX=0 NormalY=0 NormalZ=1 AngleXU=0 Radius=3 StartAngle=4.71239 EndAngle=6.28319
    g6: ArcOfCircle CenterX=7.08745 CenterY=1.38411 CenterZ=0 NormalX=0 NormalY=0 NormalZ=1 AngleXU=0 Radius=1 StartAngle=5.35e-14 EndAngle=1.5708
    g7: LineSegment StartX=10.0875 StartY=-1.11588 StartZ=0 EndX=10.0875 EndY=1.38411 EndZ=0
    g8: ArcOfCircle CenterX=7.08745 CenterY=1.38411 CenterZ=0 NormalX=0 NormalY=0 NormalZ=1 AngleXU=0 Radius=3 StartAngle=3.57e-14 EndAngle=1.5708
    g9: ArcOfCircle CenterX=4.58745 CenterY=1.38412 CenterZ=0 NormalX=0 NormalY=0 NormalZ=1 AngleXU=0 Radius=1 StartAngle=1.57081 EndAngle=3.14159
    g10: LineSegment StartX=4.58744 StartY=2.38411 StartZ=0 EndX=7.08745 EndY=2.38411 EndZ=0
    g11: LineSegment StartX=4.58745 StartY=4.38411 StartZ=0 EndX=7.08745 EndY=4.38411 EndZ=0
    g12: ArcOfCircle CenterX=4.58745 CenterY=5.38411 CenterZ=0 NormalX=0 NormalY=0 NormalZ=1 AngleXU=0 Radius=1 StartAngle=3.14159 EndAngle=4.71239
    g13: LineSegment StartX=3.58745 StartY=5.38411 StartZ=0 EndX=3.58745 EndY=1.38411 EndZ=0
  constraints (33):
    c: Vertical(g0)
    c: Block(g0)
    c: Block(g1)
    c: Coincident(g2,g1)
    c: Coincident(g3,g0)
    c: Coincident(g3,g2)
    c: Horizontal(g3)
    c: Block(g2)
    c: Coincident(g4,g0)
    c: Horizontal(g4)
    c: Coincident(g5,g2)
    c: Block(g5)
    c: Block(g4)
    c: Coincident(g6,g1)
    c: Block(g6)
    c: Coincident(g7,g5)
    c: Vertical(g7)
    c: Coincident(g8,g6)
    c: Block(g8)
    c: Block(g7)
    c: Coincident(g10,g9)
    c: Coincident(g10,g6)
    c: Horizontal(g10)
    c: Block(g10)
    c: Block(g9)
    c: Coincident(g11,g8)
    c: Horizontal(g11)
    c: Block(g12)
    c: Block(g11)
    c: Coincident(g13,g12)
    c: Coincident(g13,g9)
    c: Vertical(g13)
    c: Tangent(g13,g9)
FEATURE [Part::Extrusion] Extrude041
  Base = -> Sketch049
  Dir = (1,0,0)
  DirMode = 2
  FaceMakerClass = Part::FaceMakerBullseye
  LengthFwd = 10
  LengthRev = 0
  Placement = pos=(-2,-22.615,14.6) rot=(0,0,1;3.14159rad)
  Solid = true
  Symmetric = false
FEATURE [Part::MultiFuse] Fusion023
  Shapes = -> [Extrude039,Extrude040,Extrude041,Cut014,Fusion015]
FEATURE [Part::Extrusion] Extrude042
  Base = -> Sketch034
  Dir = (0,0.894389,-0.447291)
  DirMode = 2
  FaceMakerClass = Part::FaceMakerBullseye
  LengthFwd = 14
  LengthRev = 0
  Placement = pos=(45.5,-14,11) rot=(1,0,0;0.466003rad)
  Solid = true
  Symmetric = false
FEATURE [Part::Fillet] Fillet021
  Base = -> Extrude042
  Edges = 1 edges r=1.95: [Edge2]
FEATURE [Part::Fillet] Fillet022
  Base = -> Fillet021
  Edges = 1 edges r=1.9: [Edge12]
  Placement = pos=(0,0,0.6) rot=(0,0,1;0rad)
FEATURE [Part::Box] Box014  label="Cube014"
  AttacherType = Attacher::AttachEngine3D
  Height = 2
  Length = 2
  Placement = pos=(-12.85,-28.2,0) rot=(0,0,1;0rad)
  Width = 2
FEATURE [App::MeasureDistance] Distance005  label="Distance: 15.50 mm"
  Distance = 15.5
  P1 = (-17.5,-32.7025,2.99911)
  P2 = (-2,-32.7025,2.99911)
FEATURE [Part::Box] Box015  label="Cube015"
  AttacherType = Attacher::AttachEngine3D
  Height = 2
  Length = 2
  Placement = pos=(-10.85,-28.2,0) rot=(0,0,1;0rad)
  Width = 2
FEATURE [Part::MultiFuse] Fusion024  label="wireHoldersecondery024"
  Placement = pos=(-8.65,0,10.48) rot=(0,0,1;0rad)
  Shapes = -> [Box015,Box014]
FEATURE [App::MeasureDistance] Distance006  label="Distance: 9.44 mm"
  Distance = 9.44274
  P1 = (-8.85,-28.2,0)
  P2 = (-2,-28.1337,6.49911)
FEATURE [Part::Box] Box016  label="Cube016"
  AttacherType = Attacher::AttachEngine3D
  Height = 2
  Length = 2
  Placement = pos=(-12.85,-28.2,0) rot=(0,0,1;0rad)
  Width = 2
FEATURE [Part::Box] Box017  label="Cube017"
  AttacherType = Attacher::AttachEngine3D
  Height = 2
  Length = 2
  Placement = pos=(-10.85,-28.2,0) rot=(0,0,1;0rad)
  Width = 2
FEATURE [Part::MultiFuse] Fusion025  label="wireHoldersecondery025"
  Placement = pos=(1,0,0) rot=(0,0,1;0rad)
  Shapes = -> [Box017,Box016]
FEATURE [App::MeasureDistance] Distance007  label="Distance: 1.58 mm"
  Distance = 1.582
  P1 = (-12,-28.7025,10.4841)
  P2 = (-13.5,-28.2,10.5)
FEATURE [App::MeasureDistance] Distance008  label="Distance: 1.58 mm001"
  Distance = 1.58193
  P1 = (-13.5,-28.2,10.49)
  P2 = (-12,-28.7025,10.4841)
FEATURE [App::MeasureDistance] Distance009  label="Distance: 1.58 mm002"
  Distance = 1.58192
  P1 = (-13.5,-28.2,10.48)
  P2 = (-12,-28.7025,10.4841)
